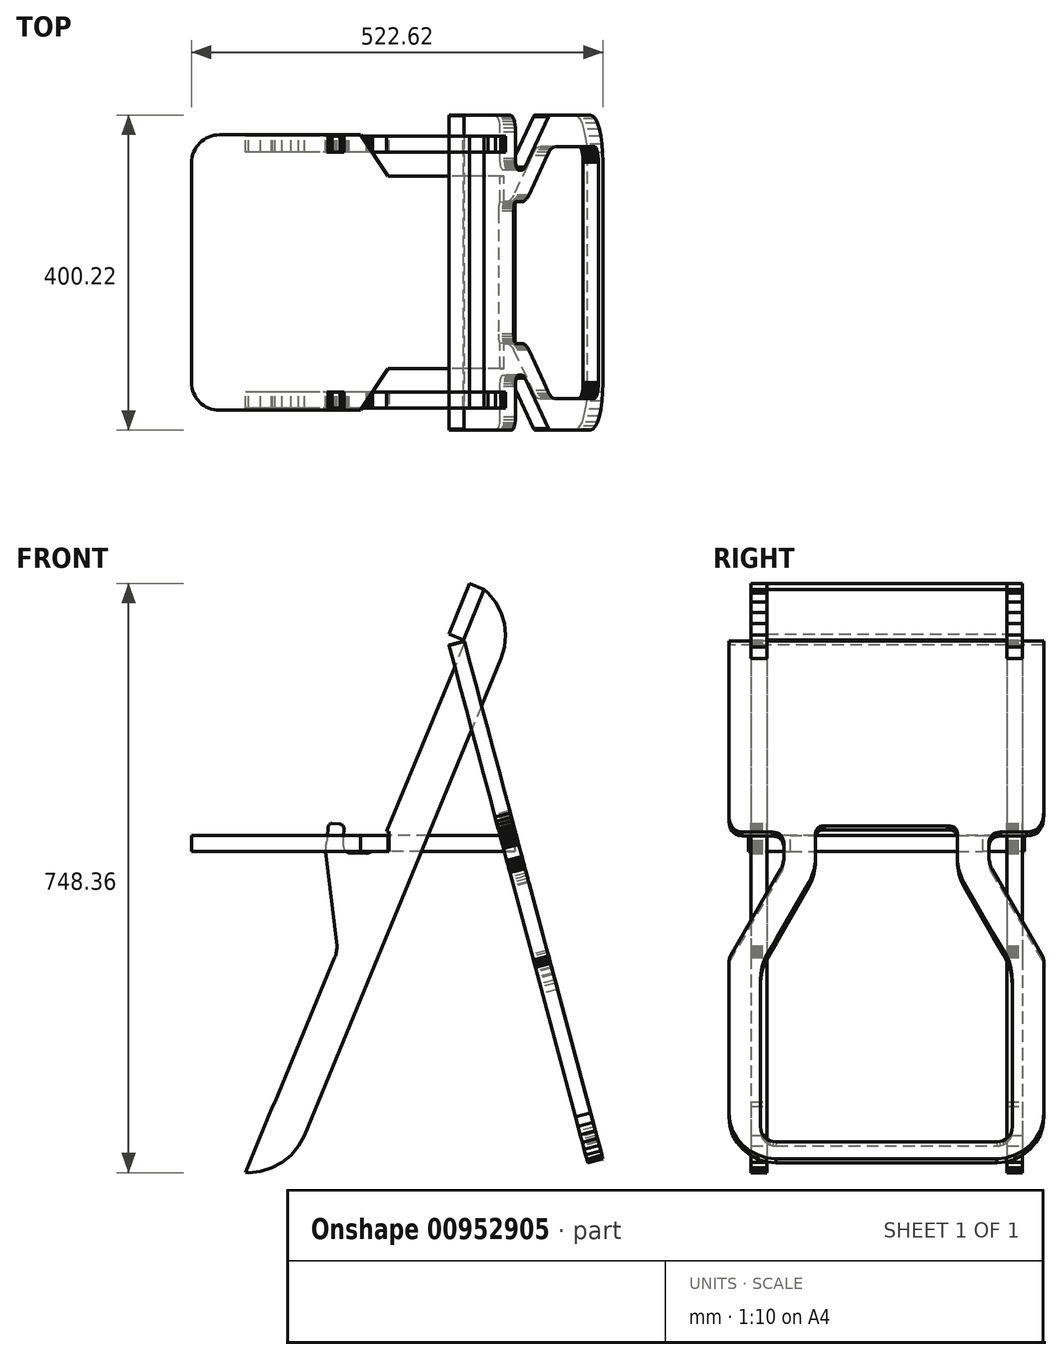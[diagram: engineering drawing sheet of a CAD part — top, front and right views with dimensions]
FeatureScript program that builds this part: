
annotation { "Feature Type Name" : "Feature", "Feature Type Description" : "" }
export const myFeature = defineFeature(function(context is Context, id is Id, definition is map)
    precondition{}
    {
        {
            var Q0;
            Q0=qCreatedBy(makeId("Front.planeOp"),FACE);
            var sketch = newSketch(context, id + "F0", { "sketchPlane" : qUnion([Q0])});
            skLineSegment(sketch, "E0", {"start": v(2007.17, 404.06) * mm, "end": v(2013.51, 402.08) * mm});
            skLineSegment(sketch, "E1", {"start": v(2013.51, 402.08) * mm, "end": v(2026.6, 394.95) * mm});
            skLineSegment(sketch, "E2", {"start": v(2026.6, 394.95) * mm, "end": v(2038.03, 385.51) * mm});
            skLineSegment(sketch, "E3", {"start": v(2038.03, 385.51) * mm, "end": v(2047.46, 374.1) * mm});
            skLineSegment(sketch, "E4", {"start": v(2047.46, 374.1) * mm, "end": v(2054.6, 361) * mm});
            skLineSegment(sketch, "E5", {"start": v(2054.6, 361) * mm, "end": v(2059.1, 346.55) * mm});
            skLineSegment(sketch, "E6", {"start": v(2059.1, 346.55) * mm, "end": v(2060.68, 331.06) * mm});
            skLineSegment(sketch, "E7", {"start": v(2060.68, 331.06) * mm, "end": v(2060.68, -323.77) * mm});
            skLineSegment(sketch, "E8", {"start": v(2060.68, -323.77) * mm, "end": v(2059.1, -339.25) * mm});
            skLineSegment(sketch, "E9", {"start": v(2059.1, -339.25) * mm, "end": v(2054.6, -353.7) * mm});
            skLineSegment(sketch, "E10", {"start": v(2054.6, -353.7) * mm, "end": v(2047.46, -366.8) * mm});
            skLineSegment(sketch, "E11", {"start": v(2047.46, -366.8) * mm, "end": v(2038.03, -378.22) * mm});
            skLineSegment(sketch, "E12", {"start": v(2038.03, -378.22) * mm, "end": v(2026.6, -387.65) * mm});
            skLineSegment(sketch, "E13", {"start": v(2026.6, -387.65) * mm, "end": v(2013.51, -394.78) * mm});
            skLineSegment(sketch, "E14", {"start": v(2013.51, -394.78) * mm, "end": v(2009.8, -395.94) * mm});
            skLineSegment(sketch, "E15", {"start": v(2010.11, -100.23) * mm, "end": v(2010.11, -299.15) * mm});
            skLineSegment(sketch, "E16", {"start": v(2010.11, -299.15) * mm, "end": v(2009.5, -305.2) * mm});
            skLineSegment(sketch, "E17", {"start": v(2007.4, 334.75) * mm, "end": v(2008.19, 333.78) * mm});
            skLineSegment(sketch, "E18", {"start": v(2008.19, 333.78) * mm, "end": v(2009.23, 331.88) * mm});
            skLineSegment(sketch, "E19", {"start": v(2009.23, 331.88) * mm, "end": v(2009.88, 329.78) * mm});
            skLineSegment(sketch, "E20", {"start": v(2009.88, 329.78) * mm, "end": v(2010.11, 327.52) * mm});
            skLineSegment(sketch, "E21", {"start": v(2010.11, 327.52) * mm, "end": v(2010.11, 68.34) * mm});
            skLineSegment(sketch, "E22", {"start": v(2010.11, 68.34) * mm, "end": v(2010.11, 63.22) * mm});
            skLineSegment(sketch, "E23", {"start": v(2010.11, 63.22) * mm, "end": v(2009.48, 58) * mm});
            skLineSegment(sketch, "E24", {"start": v(2009.48, 58) * mm, "end": v(2008.29, 52.92) * mm});
            skLineSegment(sketch, "E25", {"start": v(2008.29, 52.92) * mm, "end": v(2006.6, 48.23) * mm});
            skLineSegment(sketch, "E26", {"start": v(2006.6, 48.23) * mm, "end": v(2004.45, 44.16) * mm});
            skLineSegment(sketch, "E27", {"start": v(2004.45, 44.16) * mm, "end": v(2001.94, 40.95) * mm});
            skLineSegment(sketch, "E28", {"start": v(2001.94, 40.95) * mm, "end": v(1999.1, 38.85) * mm});
            skLineSegment(sketch, "E29", {"start": v(1999.1, 38.85) * mm, "end": v(1996.98, 37.37) * mm});
            skLineSegment(sketch, "E30", {"start": v(1996.98, 37.37) * mm, "end": v(1976.11, 29) * mm});
            skLineSegment(sketch, "E31", {"start": v(1976.11, 29) * mm, "end": v(1973.5, 29.28) * mm});
            skLineSegment(sketch, "E32", {"start": v(1973.5, 29.28) * mm, "end": v(1971.2, 30.06) * mm});
            skLineSegment(sketch, "E33", {"start": v(1971.2, 30.06) * mm, "end": v(1969.22, 31.28) * mm});
            skLineSegment(sketch, "E34", {"start": v(1969.22, 31.28) * mm, "end": v(1967.59, 32.9) * mm});
            skLineSegment(sketch, "E35", {"start": v(1967.59, 32.9) * mm, "end": v(1966.3, 34.84) * mm});
            skLineSegment(sketch, "E36", {"start": v(1966.3, 34.84) * mm, "end": v(1965.37, 37.06) * mm});
            skLineSegment(sketch, "E37", {"start": v(1965.37, 37.06) * mm, "end": v(1958.88, 54.54) * mm});
            skLineSegment(sketch, "E38", {"start": v(1958.88, 54.54) * mm, "end": v(1958.2, 55.86) * mm});
            skLineSegment(sketch, "E39", {"start": v(1958.2, 55.86) * mm, "end": v(1957.45, 56.96) * mm});
            skLineSegment(sketch, "E40", {"start": v(1957.45, 56.96) * mm, "end": v(1956.64, 57.82) * mm});
            skLineSegment(sketch, "E41", {"start": v(1956.64, 57.82) * mm, "end": v(1955.76, 58.45) * mm});
            skLineSegment(sketch, "E42", {"start": v(1955.76, 58.45) * mm, "end": v(1954.82, 58.85) * mm});
            skLineSegment(sketch, "E43", {"start": v(1954.82, 58.85) * mm, "end": v(1953.8, 59.02) * mm});
            skLineSegment(sketch, "E44", {"start": v(1953.8, 59.02) * mm, "end": v(1952.73, 58.96) * mm});
            skLineSegment(sketch, "E45", {"start": v(1952.73, 58.96) * mm, "end": v(1951.59, 58.66) * mm});
            skLineSegment(sketch, "E46", {"start": v(1951.59, 58.66) * mm, "end": v(1942.33, 55.68) * mm});
            skLineSegment(sketch, "E47", {"start": v(1942.33, 55.68) * mm, "end": v(1941.28, 55.24) * mm});
            skLineSegment(sketch, "E48", {"start": v(1941.28, 55.24) * mm, "end": v(1940.44, 54.66) * mm});
            skLineSegment(sketch, "E49", {"start": v(1940.44, 54.66) * mm, "end": v(1939.8, 53.91) * mm});
            skLineSegment(sketch, "E50", {"start": v(1939.8, 53.91) * mm, "end": v(1939.39, 53.02) * mm});
            skLineSegment(sketch, "E51", {"start": v(1939.39, 53.02) * mm, "end": v(1939.17, 51.97) * mm});
            skLineSegment(sketch, "E52", {"start": v(1939.17, 51.97) * mm, "end": v(1939.15, 50.78) * mm});
            skLineSegment(sketch, "E53", {"start": v(1939.15, 50.78) * mm, "end": v(1939.33, 49.45) * mm});
            skLineSegment(sketch, "E54", {"start": v(1939.33, 49.45) * mm, "end": v(1939.7, 47.98) * mm});
            skLineSegment(sketch, "E55", {"start": v(1939.7, 47.98) * mm, "end": v(1944.4, 33.38) * mm});
            skLineSegment(sketch, "E56", {"start": v(1944.4, 33.38) * mm, "end": v(1944.5, 31.68) * mm});
            skLineSegment(sketch, "E57", {"start": v(1944.5, 31.68) * mm, "end": v(1944.7, 30.05) * mm});
            skLineSegment(sketch, "E58", {"start": v(1944.7, 30.05) * mm, "end": v(1944.96, 28.48) * mm});
            skLineSegment(sketch, "E59", {"start": v(1944.96, 28.48) * mm, "end": v(1945.29, 26.96) * mm});
            skLineSegment(sketch, "E60", {"start": v(1945.29, 26.96) * mm, "end": v(1945.68, 25.5) * mm});
            skLineSegment(sketch, "E61", {"start": v(1945.68, 25.5) * mm, "end": v(1946.8, 22.9) * mm});
            skLineSegment(sketch, "E62", {"start": v(1946.8, 22.9) * mm, "end": v(1947.33, 21.55) * mm});
            skLineSegment(sketch, "E63", {"start": v(1947.33, 21.55) * mm, "end": v(1948.2, 19.6) * mm});
            skLineSegment(sketch, "E64", {"start": v(1948.2, 19.6) * mm, "end": v(2007.08, -85.78) * mm});
            skLineSegment(sketch, "E65", {"start": v(2007.08, -85.78) * mm, "end": v(2007.77, -87.31) * mm});
            skLineSegment(sketch, "E66", {"start": v(2007.77, -87.31) * mm, "end": v(2008.37, -88.92) * mm});
            skLineSegment(sketch, "E67", {"start": v(2008.37, -88.92) * mm, "end": v(2008.89, -90.61) * mm});
            skLineSegment(sketch, "E68", {"start": v(2008.89, -90.61) * mm, "end": v(2009.3, -92.38) * mm});
            skLineSegment(sketch, "E69", {"start": v(2009.3, -92.38) * mm, "end": v(2009.64, -94.23) * mm});
            skLineSegment(sketch, "E70", {"start": v(2009.64, -94.23) * mm, "end": v(2009.88, -96.15) * mm});
            skLineSegment(sketch, "E71", {"start": v(2009.88, -96.15) * mm, "end": v(2010.04, -98.16) * mm});
            skLineSegment(sketch, "E72", {"start": v(2010.04, -98.16) * mm, "end": v(2010.11, -100.23) * mm});
            skLineSegment(sketch, "E73", {"start": v(2007.17, 404.06) * mm, "end": v(2007.4, 334.75) * mm});
            skLineSegment(sketch, "E74.trimOffspring", {"start": v(2009.5, -305.2) * mm, "end": v(2009.8, -395.94) * mm});
            skSolve(sketch);
        }
        {
            var Q0;
            Q0=makeQuery(id+"F0.imprint","IMPRINT",FACE,{"disambiguationData":[TD([[makeQuery(id+"F0.imprint","IMPRINT",EDGE,{"derivedFrom":sQuery(id+"F0.wireOp",EDGE,"E0")}),-1.0]])]});
            extrude(context, id + "F1", {"entities" : qUnion([Q0]), "depth" : 20 * mm, "offsetDistance" : 25 * mm});
        }
        {
            var Q0;
            Q0=makeQuery(id+"F1.opExtrude","SWEPT_BODY",BODY,{"disambiguationData":[OSD([sQuery(id+"F0.wireOp",EDGE,"E0"),sQuery(id+"F0.wireOp",EDGE,"E1"),sQuery(id+"F0.wireOp",EDGE,"E2"),sQuery(id+"F0.wireOp",EDGE,"E3"),sQuery(id+"F0.wireOp",EDGE,"E4"),sQuery(id+"F0.wireOp",EDGE,"E5"),sQuery(id+"F0.wireOp",EDGE,"E6"),sQuery(id+"F0.wireOp",EDGE,"E7"),sQuery(id+"F0.wireOp",EDGE,"E8"),sQuery(id+"F0.wireOp",EDGE,"E9"),sQuery(id+"F0.wireOp",EDGE,"E10"),sQuery(id+"F0.wireOp",EDGE,"E11"),sQuery(id+"F0.wireOp",EDGE,"E12"),sQuery(id+"F0.wireOp",EDGE,"E13"),sQuery(id+"F0.wireOp",EDGE,"E14"),sQuery(id+"F0.wireOp",EDGE,"E15"),sQuery(id+"F0.wireOp",EDGE,"E16"),sQuery(id+"F0.wireOp",EDGE,"E17"),sQuery(id+"F0.wireOp",EDGE,"E18"),sQuery(id+"F0.wireOp",EDGE,"E19"),sQuery(id+"F0.wireOp",EDGE,"E20"),sQuery(id+"F0.wireOp",EDGE,"E21"),sQuery(id+"F0.wireOp",EDGE,"E22"),sQuery(id+"F0.wireOp",EDGE,"E23"),sQuery(id+"F0.wireOp",EDGE,"E24"),sQuery(id+"F0.wireOp",EDGE,"E25"),sQuery(id+"F0.wireOp",EDGE,"E26"),sQuery(id+"F0.wireOp",EDGE,"E27"),sQuery(id+"F0.wireOp",EDGE,"E28"),sQuery(id+"F0.wireOp",EDGE,"E29"),sQuery(id+"F0.wireOp",EDGE,"E30"),sQuery(id+"F0.wireOp",EDGE,"E31"),sQuery(id+"F0.wireOp",EDGE,"E32"),sQuery(id+"F0.wireOp",EDGE,"E33"),sQuery(id+"F0.wireOp",EDGE,"E34"),sQuery(id+"F0.wireOp",EDGE,"E35"),sQuery(id+"F0.wireOp",EDGE,"E36"),sQuery(id+"F0.wireOp",EDGE,"bf83b80b-95e6-45bf-b00d-f85eb3b2e45b"),sQuery(id+"F0.wireOp",EDGE,"3aedeaf8-a7c8-49c8-8eb8-d34febc41528"),sQuery(id+"F0.wireOp",EDGE,"E37"),sQuery(id+"F0.wireOp",EDGE,"E38"),sQuery(id+"F0.wireOp",EDGE,"E39"),sQuery(id+"F0.wireOp",EDGE,"E40"),sQuery(id+"F0.wireOp",EDGE,"E41"),sQuery(id+"F0.wireOp",EDGE,"E42"),sQuery(id+"F0.wireOp",EDGE,"E43"),sQuery(id+"F0.wireOp",EDGE,"E44"),sQuery(id+"F0.wireOp",EDGE,"E45"),sQuery(id+"F0.wireOp",EDGE,"E46"),sQuery(id+"F0.wireOp",EDGE,"E47"),sQuery(id+"F0.wireOp",EDGE,"E48"),sQuery(id+"F0.wireOp",EDGE,"E49"),sQuery(id+"F0.wireOp",EDGE,"E50"),sQuery(id+"F0.wireOp",EDGE,"E51"),sQuery(id+"F0.wireOp",EDGE,"E52"),sQuery(id+"F0.wireOp",EDGE,"E53"),sQuery(id+"F0.wireOp",EDGE,"E54"),sQuery(id+"F0.wireOp",EDGE,"E55"),sQuery(id+"F0.wireOp",EDGE,"E56"),sQuery(id+"F0.wireOp",EDGE,"E57"),sQuery(id+"F0.wireOp",EDGE,"E58"),sQuery(id+"F0.wireOp",EDGE,"E59"),sQuery(id+"F0.wireOp",EDGE,"E60"),sQuery(id+"F0.wireOp",EDGE,"E61"),sQuery(id+"F0.wireOp",EDGE,"E62"),sQuery(id+"F0.wireOp",EDGE,"E63"),sQuery(id+"F0.wireOp",EDGE,"E64"),sQuery(id+"F0.wireOp",EDGE,"E65"),sQuery(id+"F0.wireOp",EDGE,"E66"),sQuery(id+"F0.wireOp",EDGE,"E67"),sQuery(id+"F0.wireOp",EDGE,"E68"),sQuery(id+"F0.wireOp",EDGE,"E69"),sQuery(id+"F0.wireOp",EDGE,"E70"),sQuery(id+"F0.wireOp",EDGE,"E71"),sQuery(id+"F0.wireOp",EDGE,"E72"),sQuery(id+"F0.wireOp",EDGE,"E73"),sQuery(id+"F0.wireOp",EDGE,"E74.trimOffspring")])]});
            var Q1;
            Q1=makeQuery(id+"F1.opExtrude","SWEPT_EDGE",EDGE,{"disambiguationData":[OSD([sQuery(id+"F0.wireOp",EDGE,"E14"),sQuery(id+"F0.wireOp",EDGE,"E74.trimOffspring")])]});
            transform(context, id + "F2", {"entities" : qUnion([Q0]), "transformType" : TransformType.ROTATION, "transformAxis" : qUnion([Q1]), "angle" : 0.4 * radian, "makeCopy" : false});
        }
        {
            var Q0;
            Q0=makeQuery(id+"F1.opExtrude","SWEPT_BODY",BODY,{"disambiguationData":[OSD([sQuery(id+"F0.wireOp",EDGE,"E0"),sQuery(id+"F0.wireOp",EDGE,"E1"),sQuery(id+"F0.wireOp",EDGE,"E2"),sQuery(id+"F0.wireOp",EDGE,"E3"),sQuery(id+"F0.wireOp",EDGE,"E4"),sQuery(id+"F0.wireOp",EDGE,"E5"),sQuery(id+"F0.wireOp",EDGE,"E6"),sQuery(id+"F0.wireOp",EDGE,"E7"),sQuery(id+"F0.wireOp",EDGE,"E8"),sQuery(id+"F0.wireOp",EDGE,"E9"),sQuery(id+"F0.wireOp",EDGE,"E10"),sQuery(id+"F0.wireOp",EDGE,"E11"),sQuery(id+"F0.wireOp",EDGE,"E12"),sQuery(id+"F0.wireOp",EDGE,"E13"),sQuery(id+"F0.wireOp",EDGE,"E14"),sQuery(id+"F0.wireOp",EDGE,"E15"),sQuery(id+"F0.wireOp",EDGE,"E16"),sQuery(id+"F0.wireOp",EDGE,"E17"),sQuery(id+"F0.wireOp",EDGE,"E18"),sQuery(id+"F0.wireOp",EDGE,"E19"),sQuery(id+"F0.wireOp",EDGE,"E20"),sQuery(id+"F0.wireOp",EDGE,"E21"),sQuery(id+"F0.wireOp",EDGE,"E22"),sQuery(id+"F0.wireOp",EDGE,"E23"),sQuery(id+"F0.wireOp",EDGE,"E24"),sQuery(id+"F0.wireOp",EDGE,"E25"),sQuery(id+"F0.wireOp",EDGE,"E26"),sQuery(id+"F0.wireOp",EDGE,"E27"),sQuery(id+"F0.wireOp",EDGE,"E28"),sQuery(id+"F0.wireOp",EDGE,"E29"),sQuery(id+"F0.wireOp",EDGE,"E30"),sQuery(id+"F0.wireOp",EDGE,"E31"),sQuery(id+"F0.wireOp",EDGE,"E32"),sQuery(id+"F0.wireOp",EDGE,"E33"),sQuery(id+"F0.wireOp",EDGE,"E34"),sQuery(id+"F0.wireOp",EDGE,"E35"),sQuery(id+"F0.wireOp",EDGE,"E36"),sQuery(id+"F0.wireOp",EDGE,"bf83b80b-95e6-45bf-b00d-f85eb3b2e45b"),sQuery(id+"F0.wireOp",EDGE,"3aedeaf8-a7c8-49c8-8eb8-d34febc41528"),sQuery(id+"F0.wireOp",EDGE,"E37"),sQuery(id+"F0.wireOp",EDGE,"E38"),sQuery(id+"F0.wireOp",EDGE,"E39"),sQuery(id+"F0.wireOp",EDGE,"E40"),sQuery(id+"F0.wireOp",EDGE,"E41"),sQuery(id+"F0.wireOp",EDGE,"E42"),sQuery(id+"F0.wireOp",EDGE,"E43"),sQuery(id+"F0.wireOp",EDGE,"E44"),sQuery(id+"F0.wireOp",EDGE,"E45"),sQuery(id+"F0.wireOp",EDGE,"E46"),sQuery(id+"F0.wireOp",EDGE,"E47"),sQuery(id+"F0.wireOp",EDGE,"E48"),sQuery(id+"F0.wireOp",EDGE,"E49"),sQuery(id+"F0.wireOp",EDGE,"E50"),sQuery(id+"F0.wireOp",EDGE,"E51"),sQuery(id+"F0.wireOp",EDGE,"E52"),sQuery(id+"F0.wireOp",EDGE,"E53"),sQuery(id+"F0.wireOp",EDGE,"E54"),sQuery(id+"F0.wireOp",EDGE,"E55"),sQuery(id+"F0.wireOp",EDGE,"E56"),sQuery(id+"F0.wireOp",EDGE,"E57"),sQuery(id+"F0.wireOp",EDGE,"E58"),sQuery(id+"F0.wireOp",EDGE,"E59"),sQuery(id+"F0.wireOp",EDGE,"E60"),sQuery(id+"F0.wireOp",EDGE,"E61"),sQuery(id+"F0.wireOp",EDGE,"E62"),sQuery(id+"F0.wireOp",EDGE,"E63"),sQuery(id+"F0.wireOp",EDGE,"E64"),sQuery(id+"F0.wireOp",EDGE,"E65"),sQuery(id+"F0.wireOp",EDGE,"E66"),sQuery(id+"F0.wireOp",EDGE,"E67"),sQuery(id+"F0.wireOp",EDGE,"E68"),sQuery(id+"F0.wireOp",EDGE,"E69"),sQuery(id+"F0.wireOp",EDGE,"E70"),sQuery(id+"F0.wireOp",EDGE,"E71"),sQuery(id+"F0.wireOp",EDGE,"E72"),sQuery(id+"F0.wireOp",EDGE,"E73"),sQuery(id+"F0.wireOp",EDGE,"E74.trimOffspring")])]});
            transform(context, id + "F3", {"entities" : qUnion([Q0]), "transformType" : TransformType.TRANSLATION_3D, "dx" : -2060 * mm, "dy" : 0 * mm, "dz" : 0 * mm, "makeCopy" : false});
        }
        {
            var Q0;
            Q0=qCreatedBy(makeId("Top.planeOp"),FACE);
            cPlane(context, id + "F4", {"entities" : qUnion([Q0]), "cplaneType" : CPlaneType.OFFSET, "offset" : 12 * mm, "width" : 150 * mm, "height" : 150 * mm});
        }
        {
            var Q0;
            Q0=qCreatedBy(id+"F4.planeOp",FACE);
            var sketch = newSketch(context, id + "F5", { "sketchPlane" : qUnion([Q0])});
            skLineSegment(sketch, "E75.bottom", {"start": v(95.33, 327) * mm, "end": v(-83.33, 327) * mm});
            skLineSegment(sketch, "E75.top", {"start": v(95.33, -23) * mm, "end": v(-83.33, -23) * mm});
            skLineSegment(sketch, "E75.left", {"start": v(131, 291.33) * mm, "end": v(131, 12.67) * mm});
            skLineSegment(sketch, "E75.right", {"start": v(-119, 291.33) * mm, "end": v(-119, 12.67) * mm});
            skPoint(sketch, "E76.visualSharp", {"position": v(-119, 327) * mm});
            skArc(sketch, "E76.filletArc", {"start": v(-83.33, 327) * mm, "mid": v(-108.55, 316.55) * mm, "end": v(-119, 291.33) * mm});
            skPoint(sketch, "E77.visualSharp", {"position": v(131, 327) * mm});
            skArc(sketch, "E77.filletArc", {"start": v(131, 291.33) * mm, "mid": v(120.55, 316.55) * mm, "end": v(95.33, 327) * mm});
            skPoint(sketch, "E78.visualSharp", {"position": v(131, -23) * mm});
            skArc(sketch, "E78.filletArc", {"start": v(95.33, -23) * mm, "mid": v(120.55, -12.55) * mm, "end": v(131, 12.67) * mm});
            skPoint(sketch, "E79.visualSharp", {"position": v(-119, -23) * mm});
            skArc(sketch, "E79.filletArc", {"start": v(-119, 12.67) * mm, "mid": v(-108.55, -12.55) * mm, "end": v(-83.33, -23) * mm});
            skSolve(sketch);
        }
        {
            var Q0;
            Q0=makeQuery(id+"F5.imprint","IMPRINT",FACE,{"disambiguationData":[TD([[makeQuery(id+"F5.imprint","IMPRINT",EDGE,{"derivedFrom":sQuery(id+"F5.wireOp",EDGE,"E75.bottom")}),1.0]])]});
            extrude(context, id + "F6", {"entities" : qUnion([Q0]), "depth" : 20 * mm, "offsetDistance" : 25 * mm});
        }
        {
            var Q0;
            Q0=makeQuery(id+"F1.opExtrude","SWEPT_BODY",BODY,{"disambiguationData":[OSD([sQuery(id+"F0.wireOp",EDGE,"E0"),sQuery(id+"F0.wireOp",EDGE,"E1"),sQuery(id+"F0.wireOp",EDGE,"E2"),sQuery(id+"F0.wireOp",EDGE,"E3"),sQuery(id+"F0.wireOp",EDGE,"E4"),sQuery(id+"F0.wireOp",EDGE,"E5"),sQuery(id+"F0.wireOp",EDGE,"E6"),sQuery(id+"F0.wireOp",EDGE,"E7"),sQuery(id+"F0.wireOp",EDGE,"E8"),sQuery(id+"F0.wireOp",EDGE,"E9"),sQuery(id+"F0.wireOp",EDGE,"E10"),sQuery(id+"F0.wireOp",EDGE,"E11"),sQuery(id+"F0.wireOp",EDGE,"E12"),sQuery(id+"F0.wireOp",EDGE,"E13"),sQuery(id+"F0.wireOp",EDGE,"E14"),sQuery(id+"F0.wireOp",EDGE,"E15"),sQuery(id+"F0.wireOp",EDGE,"E16"),sQuery(id+"F0.wireOp",EDGE,"E17"),sQuery(id+"F0.wireOp",EDGE,"E18"),sQuery(id+"F0.wireOp",EDGE,"E19"),sQuery(id+"F0.wireOp",EDGE,"E20"),sQuery(id+"F0.wireOp",EDGE,"E21"),sQuery(id+"F0.wireOp",EDGE,"E22"),sQuery(id+"F0.wireOp",EDGE,"E23"),sQuery(id+"F0.wireOp",EDGE,"E24"),sQuery(id+"F0.wireOp",EDGE,"E25"),sQuery(id+"F0.wireOp",EDGE,"E26"),sQuery(id+"F0.wireOp",EDGE,"E27"),sQuery(id+"F0.wireOp",EDGE,"E28"),sQuery(id+"F0.wireOp",EDGE,"E29"),sQuery(id+"F0.wireOp",EDGE,"E30"),sQuery(id+"F0.wireOp",EDGE,"E31"),sQuery(id+"F0.wireOp",EDGE,"E32"),sQuery(id+"F0.wireOp",EDGE,"E33"),sQuery(id+"F0.wireOp",EDGE,"E34"),sQuery(id+"F0.wireOp",EDGE,"E35"),sQuery(id+"F0.wireOp",EDGE,"E36"),sQuery(id+"F0.wireOp",EDGE,"E37"),sQuery(id+"F0.wireOp",EDGE,"E38"),sQuery(id+"F0.wireOp",EDGE,"E39"),sQuery(id+"F0.wireOp",EDGE,"E40"),sQuery(id+"F0.wireOp",EDGE,"E41"),sQuery(id+"F0.wireOp",EDGE,"E42"),sQuery(id+"F0.wireOp",EDGE,"E43"),sQuery(id+"F0.wireOp",EDGE,"E44"),sQuery(id+"F0.wireOp",EDGE,"E45"),sQuery(id+"F0.wireOp",EDGE,"E46"),sQuery(id+"F0.wireOp",EDGE,"E47"),sQuery(id+"F0.wireOp",EDGE,"E48"),sQuery(id+"F0.wireOp",EDGE,"E49"),sQuery(id+"F0.wireOp",EDGE,"E50"),sQuery(id+"F0.wireOp",EDGE,"E51"),sQuery(id+"F0.wireOp",EDGE,"E52"),sQuery(id+"F0.wireOp",EDGE,"E53"),sQuery(id+"F0.wireOp",EDGE,"E54"),sQuery(id+"F0.wireOp",EDGE,"E55"),sQuery(id+"F0.wireOp",EDGE,"E56"),sQuery(id+"F0.wireOp",EDGE,"E57"),sQuery(id+"F0.wireOp",EDGE,"E58"),sQuery(id+"F0.wireOp",EDGE,"E59"),sQuery(id+"F0.wireOp",EDGE,"E60"),sQuery(id+"F0.wireOp",EDGE,"E61"),sQuery(id+"F0.wireOp",EDGE,"E62"),sQuery(id+"F0.wireOp",EDGE,"E63"),sQuery(id+"F0.wireOp",EDGE,"E64"),sQuery(id+"F0.wireOp",EDGE,"E65"),sQuery(id+"F0.wireOp",EDGE,"E66"),sQuery(id+"F0.wireOp",EDGE,"E67"),sQuery(id+"F0.wireOp",EDGE,"E68"),sQuery(id+"F0.wireOp",EDGE,"E69"),sQuery(id+"F0.wireOp",EDGE,"E70"),sQuery(id+"F0.wireOp",EDGE,"E71"),sQuery(id+"F0.wireOp",EDGE,"E72"),sQuery(id+"F0.wireOp",EDGE,"E73"),sQuery(id+"F0.wireOp",EDGE,"E74.trimOffspring")])]});
            transform(context, id + "F7", {"entities" : qUnion([Q0]), "transformType" : TransformType.TRANSLATION_3D, "dx" : 0 * mm, "dy" : 325 * mm, "dz" : 0 * mm, "makeCopy" : true});
        }
        {
            var Q0;
            Q0=qCreatedBy(id+"F4.planeOp",FACE);
            var sketch = newSketch(context, id + "F8", { "sketchPlane" : qUnion([Q0])});
            skLineSegment(sketch, "E80", {"start": v(95.42, -22.88) * mm, "end": v(132.24, 31.84) * mm});
            skLineSegment(sketch, "E81", {"start": v(132.24, 31.84) * mm, "end": v(131.7, -45.16) * mm});
            skLineSegment(sketch, "E82", {"start": v(131.7, -45.16) * mm, "end": v(95.42, -22.88) * mm});
            skLineSegment(sketch, "E83.MirrorCS", {"start": v(132.24, 272.56) * mm, "end": v(131.7, 349.56) * mm});
            skLineSegment(sketch, "E84.MirrorCS", {"start": v(131.7, 349.56) * mm, "end": v(95.42, 327.28) * mm});
            skLineSegment(sketch, "E85.MirrorCS", {"start": v(95.42, 327.28) * mm, "end": v(132.24, 272.56) * mm});
            skSolve(sketch);
        }
        {
            var Q0;
            Q0=makeQuery(id+"F8.imprint","IMPRINT",FACE,{"disambiguationData":[TD([[makeQuery(id+"F8.imprint","IMPRINT",EDGE,{"derivedFrom":sQuery(id+"F8.wireOp",EDGE,"E80")}),-1.0]])]});
            var Q1;
            Q1=makeQuery(id+"F8.imprint","IMPRINT",FACE,{"disambiguationData":[TD([[makeQuery(id+"F8.imprint","IMPRINT",EDGE,{"derivedFrom":sQuery(id+"F8.wireOp",EDGE,"E83.MirrorCS")}),1.0]])]});
            extrude(context, id + "F9", {"entities" : qUnion([Q0, Q1]), "operationType" : NewBodyOperationType.REMOVE, "depth" : 25 * mm, "offsetDistance" : 25 * mm});
        }
        {
            var Q0;
            Q0=makeQuery(id+"F7.opPattern","COPY",FACE,{"derivedFrom":makeQuery(id+"F1.opExtrude","SWEPT_FACE",FACE,{"disambiguationData":[OSD([sQuery(id+"F0.wireOp",EDGE,"E73")])]}),"instanceName":"1"});
            var Q1;
            Q1=makeQuery(id+"F1.opExtrude","SWEPT_FACE",FACE,{"disambiguationData":[OSD([sQuery(id+"F0.wireOp",EDGE,"E73")])]});
            extrude(context, id + "F10", {"entities" : qUnion([Q0, Q1]), "depth" : 20 * mm, "offsetDistance" : 25 * mm});
        }
        {
            var Q0;
            {var subQ0=sQuery(id+"F0.wireOp",EDGE,"E73");Q0=makeQuery(id+"F10.opExtrude","SWEPT_FACE",FACE,{"disambiguationData":[OSD([subQ0]),TDD([makeQuery(id+"F1.opExtrude","CAP_EDGE",EDGE,{"disambiguationData":[OSD([subQ0])],"isStart":true})])]});}
            var Q1;
            {var subQ0=sQuery(id+"F0.wireOp",EDGE,"E73");Q1=makeQuery(id+"F10.opExtrude","SWEPT_FACE",FACE,{"disambiguationData":[OSD([subQ0]),TDD([makeQuery(id+"F7.opPattern","COPY",EDGE,{"derivedFrom":makeQuery(id+"F1.opExtrude","CAP_EDGE",EDGE,{"disambiguationData":[OSD([subQ0])],"isStart":false}),"instanceName":"1"})])]});}
            loft(context, id + "F11", {"sheetProfilesArray" : [{ "sheetProfileEntities" : qUnion([Q0]) }, { "sheetProfileEntities" : qUnion([Q1]) }]});
        }
        {
            var Q0;
            Q0=qCreatedBy(makeId("Right.planeOp"),FACE);
            var sketch = newSketch(context, id + "F12", { "sketchPlane" : qUnion([Q0])});
            skLineSegment(sketch, "E86", {"start": v(183.85, 400.19) * mm, "end": v(199.17, 398.63) * mm});
            skLineSegment(sketch, "E87", {"start": v(199.17, 398.63) * mm, "end": v(213.46, 394.17) * mm});
            skLineSegment(sketch, "E88", {"start": v(213.46, 394.17) * mm, "end": v(226.42, 387.12) * mm});
            skLineSegment(sketch, "E89", {"start": v(226.42, 387.12) * mm, "end": v(237.72, 377.78) * mm});
            skLineSegment(sketch, "E90", {"start": v(237.72, 377.78) * mm, "end": v(247.05, 366.48) * mm});
            skLineSegment(sketch, "E91", {"start": v(247.05, 366.48) * mm, "end": v(254.1, 353.53) * mm});
            skLineSegment(sketch, "E92", {"start": v(254.1, 353.53) * mm, "end": v(258.57, 339.24) * mm});
            skLineSegment(sketch, "E93", {"start": v(258.57, 339.24) * mm, "end": v(260.12, 323.91) * mm});
            skLineSegment(sketch, "E94", {"start": v(260.12, -323.91) * mm, "end": v(258.57, -339.24) * mm});
            skLineSegment(sketch, "E95", {"start": v(258.57, -339.24) * mm, "end": v(254.1, -353.53) * mm});
            skLineSegment(sketch, "E96", {"start": v(254.1, -353.53) * mm, "end": v(247.05, -366.48) * mm});
            skLineSegment(sketch, "E97", {"start": v(247.05, -366.48) * mm, "end": v(237.72, -377.78) * mm});
            skLineSegment(sketch, "E98", {"start": v(237.72, -377.78) * mm, "end": v(226.42, -387.12) * mm});
            skLineSegment(sketch, "E99", {"start": v(226.42, -387.12) * mm, "end": v(213.46, -394.17) * mm});
            skLineSegment(sketch, "E100", {"start": v(213.46, -394.17) * mm, "end": v(199.17, -398.63) * mm});
            skLineSegment(sketch, "E101", {"start": v(199.17, -398.63) * mm, "end": v(183.85, -400.19) * mm});
            skLineSegment(sketch, "E102", {"start": v(-183.85, -400.19) * mm, "end": v(-199.17, -398.63) * mm});
            skLineSegment(sketch, "E103", {"start": v(-199.17, -398.63) * mm, "end": v(-213.46, -394.17) * mm});
            skLineSegment(sketch, "E104", {"start": v(-213.46, -394.17) * mm, "end": v(-226.42, -387.12) * mm});
            skLineSegment(sketch, "E105", {"start": v(-226.42, -387.12) * mm, "end": v(-237.72, -377.78) * mm});
            skLineSegment(sketch, "E106", {"start": v(-237.72, -377.78) * mm, "end": v(-247.05, -366.48) * mm});
            skLineSegment(sketch, "E107", {"start": v(-247.05, -366.48) * mm, "end": v(-254.1, -353.53) * mm});
            skLineSegment(sketch, "E108", {"start": v(-254.1, -353.53) * mm, "end": v(-258.57, -339.24) * mm});
            skLineSegment(sketch, "E109", {"start": v(-258.57, -339.24) * mm, "end": v(-260.12, -323.91) * mm});
            skLineSegment(sketch, "E110", {"start": v(-260.12, 323.91) * mm, "end": v(-258.57, 339.24) * mm});
            skLineSegment(sketch, "E111", {"start": v(-258.57, 339.24) * mm, "end": v(-254.1, 353.53) * mm});
            skLineSegment(sketch, "E112", {"start": v(-254.1, 353.53) * mm, "end": v(-247.05, 366.48) * mm});
            skLineSegment(sketch, "E113", {"start": v(-247.05, 366.48) * mm, "end": v(-237.72, 377.78) * mm});
            skLineSegment(sketch, "E114", {"start": v(-237.72, 377.78) * mm, "end": v(-226.42, 387.12) * mm});
            skLineSegment(sketch, "E115", {"start": v(-226.42, 387.12) * mm, "end": v(-213.46, 394.17) * mm});
            skLineSegment(sketch, "E116", {"start": v(-213.46, 394.17) * mm, "end": v(-199.17, 398.63) * mm});
            skLineSegment(sketch, "E117", {"start": v(-199.17, 398.63) * mm, "end": v(-183.85, 400.19) * mm});
            skLineSegment(sketch, "E118", {"start": v(210.1, -299.56) * mm, "end": v(208.67, -313.63) * mm});
            skLineSegment(sketch, "E119", {"start": v(208.67, -313.63) * mm, "end": v(204.57, -326.75) * mm});
            skLineSegment(sketch, "E120", {"start": v(204.57, -326.75) * mm, "end": v(198.1, -338.65) * mm});
            skLineSegment(sketch, "E121", {"start": v(198.1, -338.65) * mm, "end": v(189.53, -349.02) * mm});
            skLineSegment(sketch, "E122", {"start": v(189.53, -349.02) * mm, "end": v(179.15, -357.6) * mm});
            skLineSegment(sketch, "E123", {"start": v(179.15, -357.6) * mm, "end": v(167.26, -364.07) * mm});
            skLineSegment(sketch, "E124", {"start": v(167.26, -364.07) * mm, "end": v(154.13, -368.16) * mm});
            skLineSegment(sketch, "E125", {"start": v(154.13, -368.16) * mm, "end": v(140.07, -369.6) * mm});
            skLineSegment(sketch, "E126", {"start": v(-140.07, -369.6) * mm, "end": v(-154.13, -368.16) * mm});
            skLineSegment(sketch, "E127", {"start": v(-154.13, -368.16) * mm, "end": v(-167.26, -364.07) * mm});
            skLineSegment(sketch, "E128", {"start": v(-167.26, -364.07) * mm, "end": v(-179.15, -357.6) * mm});
            skLineSegment(sketch, "E129", {"start": v(-179.15, -357.6) * mm, "end": v(-189.53, -349.02) * mm});
            skLineSegment(sketch, "E130", {"start": v(-189.53, -349.02) * mm, "end": v(-198.1, -338.65) * mm});
            skLineSegment(sketch, "E131", {"start": v(-198.1, -338.65) * mm, "end": v(-204.57, -326.75) * mm});
            skLineSegment(sketch, "E132", {"start": v(-204.57, -326.75) * mm, "end": v(-208.67, -313.63) * mm});
            skLineSegment(sketch, "E133", {"start": v(-208.67, -313.63) * mm, "end": v(-210.1, -299.56) * mm});
            skLineSegment(sketch, "E134", {"start": v(-210.1, -102.77) * mm, "end": v(-210.03, -100.72) * mm});
            skLineSegment(sketch, "E135", {"start": v(-210.03, -100.72) * mm, "end": v(-209.87, -98.74) * mm});
            skLineSegment(sketch, "E136", {"start": v(-209.87, -98.74) * mm, "end": v(-209.63, -96.83) * mm});
            skLineSegment(sketch, "E137", {"start": v(-209.63, -96.83) * mm, "end": v(-209.3, -95) * mm});
            skLineSegment(sketch, "E138", {"start": v(-209.3, -95) * mm, "end": v(-208.89, -93.25) * mm});
            skLineSegment(sketch, "E139", {"start": v(-208.89, -93.25) * mm, "end": v(-208.38, -91.58) * mm});
            skLineSegment(sketch, "E140", {"start": v(-208.38, -91.58) * mm, "end": v(-207.78, -89.99) * mm});
            skLineSegment(sketch, "E141", {"start": v(-207.78, -89.99) * mm, "end": v(-207.1, -88.47) * mm});
            skLineSegment(sketch, "E142", {"start": v(-207.1, -88.47) * mm, "end": v(-142.89, 26.6) * mm});
            skLineSegment(sketch, "E143", {"start": v(-142.89, 26.6) * mm, "end": v(-142.31, 27.88) * mm});
            skLineSegment(sketch, "E144", {"start": v(-142.31, 27.88) * mm, "end": v(-141.8, 29.22) * mm});
            skLineSegment(sketch, "E145", {"start": v(-141.8, 29.22) * mm, "end": v(-141.34, 30.61) * mm});
            skLineSegment(sketch, "E146", {"start": v(-141.34, 30.61) * mm, "end": v(-140.95, 32.06) * mm});
            skLineSegment(sketch, "E147", {"start": v(-140.95, 32.06) * mm, "end": v(-140.62, 33.56) * mm});
            skLineSegment(sketch, "E148", {"start": v(-140.62, 33.56) * mm, "end": v(-140.36, 35.11) * mm});
            skLineSegment(sketch, "E149", {"start": v(-140.36, 35.11) * mm, "end": v(-140.18, 36.73) * mm});
            skLineSegment(sketch, "E150", {"start": v(-140.18, 36.73) * mm, "end": v(-140.07, 38.4) * mm});
            skLineSegment(sketch, "E151", {"start": v(-140.07, 38.4) * mm, "end": v(-140.07, 53.59) * mm});
            skLineSegment(sketch, "E152", {"start": v(-140.07, 53.59) * mm, "end": v(-140.17, 55.08) * mm});
            skLineSegment(sketch, "E153", {"start": v(-140.17, 55.08) * mm, "end": v(-140.4, 56.39) * mm});
            skLineSegment(sketch, "E154", {"start": v(-140.4, 56.39) * mm, "end": v(-140.78, 57.5) * mm});
            skLineSegment(sketch, "E155", {"start": v(-140.78, 57.5) * mm, "end": v(-141.3, 58.42) * mm});
            skLineSegment(sketch, "E156", {"start": v(-141.3, 58.42) * mm, "end": v(-141.97, 59.13) * mm});
            skLineSegment(sketch, "E157", {"start": v(-141.97, 59.13) * mm, "end": v(-142.79, 59.64) * mm});
            skLineSegment(sketch, "E158", {"start": v(-142.79, 59.64) * mm, "end": v(-143.76, 59.94) * mm});
            skLineSegment(sketch, "E159", {"start": v(-143.76, 59.94) * mm, "end": v(-144.89, 60.03) * mm});
            skLineSegment(sketch, "E160", {"start": v(-144.89, 60.03) * mm, "end": v(-154.5, 60.03) * mm});
            skLineSegment(sketch, "E161", {"start": v(-154.5, 60.03) * mm, "end": v(-155.67, 59.96) * mm});
            skLineSegment(sketch, "E162", {"start": v(-155.67, 59.96) * mm, "end": v(-156.7, 59.7) * mm});
            skLineSegment(sketch, "E163", {"start": v(-156.7, 59.7) * mm, "end": v(-157.6, 59.23) * mm});
            skLineSegment(sketch, "E164", {"start": v(-157.6, 59.23) * mm, "end": v(-158.37, 58.57) * mm});
            skLineSegment(sketch, "E165", {"start": v(-158.37, 58.57) * mm, "end": v(-159, 57.7) * mm});
            skLineSegment(sketch, "E166", {"start": v(-159, 57.7) * mm, "end": v(-159.5, 56.65) * mm});
            skLineSegment(sketch, "E167", {"start": v(-159.5, 56.65) * mm, "end": v(-159.88, 55.4) * mm});
            skLineSegment(sketch, "E168", {"start": v(-159.88, 55.4) * mm, "end": v(-160.12, 53.94) * mm});
            skLineSegment(sketch, "E169", {"start": v(-160.12, 53.94) * mm, "end": v(-160.09, 47.06) * mm});
            skLineSegment(sketch, "E170", {"start": v(-160.09, 47.06) * mm, "end": v(-160.27, 44.47) * mm});
            skLineSegment(sketch, "E171", {"start": v(-160.27, 44.47) * mm, "end": v(-160.82, 42.05) * mm});
            skLineSegment(sketch, "E172", {"start": v(-160.82, 42.05) * mm, "end": v(-161.74, 39.85) * mm});
            skLineSegment(sketch, "E173", {"start": v(-161.74, 39.85) * mm, "end": v(-163, 37.92) * mm});
            skLineSegment(sketch, "E174", {"start": v(-163, 37.92) * mm, "end": v(-164.63, 36.33) * mm});
            skLineSegment(sketch, "E175", {"start": v(-164.63, 36.33) * mm, "end": v(-166.58, 35.12) * mm});
            skLineSegment(sketch, "E176", {"start": v(-166.58, 35.12) * mm, "end": v(-168.85, 34.35) * mm});
            skLineSegment(sketch, "E177", {"start": v(-168.85, 34.35) * mm, "end": v(-171.44, 34.08) * mm});
            skLineSegment(sketch, "E178", {"start": v(-171.44, 34.08) * mm, "end": v(-196.15, 34.08) * mm});
            skLineSegment(sketch, "E179", {"start": v(-196.15, 34.08) * mm, "end": v(-199.2, 34.82) * mm});
            skLineSegment(sketch, "E180", {"start": v(-199.2, 34.82) * mm, "end": v(-202.01, 36.9) * mm});
            skLineSegment(sketch, "E181", {"start": v(-202.01, 36.9) * mm, "end": v(-204.5, 40.08) * mm});
            skLineSegment(sketch, "E182", {"start": v(-204.5, 40.08) * mm, "end": v(-206.62, 44.1) * mm});
            skLineSegment(sketch, "E183", {"start": v(-206.62, 44.1) * mm, "end": v(-208.3, 48.75) * mm});
            skLineSegment(sketch, "E184", {"start": v(-208.3, 48.75) * mm, "end": v(-209.48, 53.77) * mm});
            skLineSegment(sketch, "E185", {"start": v(-209.48, 53.77) * mm, "end": v(-210.1, 58.93) * mm});
            skLineSegment(sketch, "E186", {"start": v(-210.1, 58.93) * mm, "end": v(-210.1, 64) * mm});
            skLineSegment(sketch, "E187", {"start": v(-210.1, 64) * mm, "end": v(-210.1, 320.41) * mm});
            skLineSegment(sketch, "E188", {"start": v(-210.1, 320.41) * mm, "end": v(-209.87, 322.64) * mm});
            skLineSegment(sketch, "E189", {"start": v(-209.87, 322.64) * mm, "end": v(-209.22, 324.72) * mm});
            skLineSegment(sketch, "E190", {"start": v(-209.22, 324.72) * mm, "end": v(-208.2, 326.6) * mm});
            skLineSegment(sketch, "E191", {"start": v(-208.2, 326.6) * mm, "end": v(-206.84, 328.25) * mm});
            skLineSegment(sketch, "E192", {"start": v(-206.84, 328.25) * mm, "end": v(-205.2, 329.6) * mm});
            skLineSegment(sketch, "E193", {"start": v(-205.2, 329.6) * mm, "end": v(-203.3, 330.64) * mm});
            skLineSegment(sketch, "E194", {"start": v(-203.3, 330.64) * mm, "end": v(-201.23, 331.29) * mm});
            skLineSegment(sketch, "E195", {"start": v(-201.23, 331.29) * mm, "end": v(-199, 331.51) * mm});
            skLineSegment(sketch, "E196", {"start": v(-199, 331.51) * mm, "end": v(199, 331.51) * mm});
            skLineSegment(sketch, "E197", {"start": v(199, 331.51) * mm, "end": v(201.23, 331.29) * mm});
            skLineSegment(sketch, "E198", {"start": v(201.23, 331.29) * mm, "end": v(203.3, 330.64) * mm});
            skLineSegment(sketch, "E199", {"start": v(203.3, 330.64) * mm, "end": v(205.2, 329.6) * mm});
            skLineSegment(sketch, "E200", {"start": v(205.2, 329.6) * mm, "end": v(206.84, 328.25) * mm});
            skLineSegment(sketch, "E201", {"start": v(206.84, 328.25) * mm, "end": v(208.2, 326.6) * mm});
            skLineSegment(sketch, "E202", {"start": v(208.2, 326.6) * mm, "end": v(209.22, 324.72) * mm});
            skLineSegment(sketch, "E203", {"start": v(209.22, 324.72) * mm, "end": v(209.87, 322.64) * mm});
            skLineSegment(sketch, "E204", {"start": v(209.87, 322.64) * mm, "end": v(210.1, 320.41) * mm});
            skLineSegment(sketch, "E205", {"start": v(210.1, 320.41) * mm, "end": v(210.1, 64) * mm});
            skLineSegment(sketch, "E206", {"start": v(210.1, 64) * mm, "end": v(210.1, 58.93) * mm});
            skLineSegment(sketch, "E207", {"start": v(210.1, 58.93) * mm, "end": v(209.48, 53.77) * mm});
            skLineSegment(sketch, "E208", {"start": v(209.48, 53.77) * mm, "end": v(208.3, 48.75) * mm});
            skLineSegment(sketch, "E209", {"start": v(208.3, 48.75) * mm, "end": v(206.62, 44.1) * mm});
            skLineSegment(sketch, "E210", {"start": v(206.62, 44.1) * mm, "end": v(204.5, 40.08) * mm});
            skLineSegment(sketch, "E211", {"start": v(204.5, 40.08) * mm, "end": v(202.01, 36.9) * mm});
            skLineSegment(sketch, "E212", {"start": v(202.01, 36.9) * mm, "end": v(199.2, 34.82) * mm});
            skLineSegment(sketch, "E213", {"start": v(199.2, 34.82) * mm, "end": v(196.15, 34.08) * mm});
            skLineSegment(sketch, "E214", {"start": v(196.15, 34.08) * mm, "end": v(171.44, 34.08) * mm});
            skLineSegment(sketch, "E215", {"start": v(171.44, 34.08) * mm, "end": v(168.85, 34.35) * mm});
            skLineSegment(sketch, "E216", {"start": v(168.85, 34.35) * mm, "end": v(166.58, 35.12) * mm});
            skLineSegment(sketch, "E217", {"start": v(166.58, 35.12) * mm, "end": v(164.63, 36.33) * mm});
            skLineSegment(sketch, "E218", {"start": v(164.63, 36.33) * mm, "end": v(163, 37.92) * mm});
            skLineSegment(sketch, "E219", {"start": v(163, 37.92) * mm, "end": v(161.74, 39.85) * mm});
            skLineSegment(sketch, "E220", {"start": v(161.74, 39.85) * mm, "end": v(160.82, 42.05) * mm});
            skLineSegment(sketch, "E221", {"start": v(160.82, 42.05) * mm, "end": v(160.27, 44.47) * mm});
            skLineSegment(sketch, "E222", {"start": v(160.27, 44.47) * mm, "end": v(160.09, 47.06) * mm});
            skLineSegment(sketch, "E223", {"start": v(160.09, 47.06) * mm, "end": v(160.12, 53.94) * mm});
            skLineSegment(sketch, "E224", {"start": v(160.12, 53.94) * mm, "end": v(159.88, 55.4) * mm});
            skLineSegment(sketch, "E225", {"start": v(159.88, 55.4) * mm, "end": v(159.5, 56.65) * mm});
            skLineSegment(sketch, "E226", {"start": v(159.5, 56.65) * mm, "end": v(159, 57.7) * mm});
            skLineSegment(sketch, "E227", {"start": v(159, 57.7) * mm, "end": v(158.37, 58.57) * mm});
            skLineSegment(sketch, "E228", {"start": v(158.37, 58.57) * mm, "end": v(157.6, 59.23) * mm});
            skLineSegment(sketch, "E229", {"start": v(157.6, 59.23) * mm, "end": v(156.7, 59.7) * mm});
            skLineSegment(sketch, "E230", {"start": v(156.7, 59.7) * mm, "end": v(155.67, 59.96) * mm});
            skLineSegment(sketch, "E231", {"start": v(155.67, 59.96) * mm, "end": v(154.5, 60.03) * mm});
            skLineSegment(sketch, "E232", {"start": v(154.5, 60.03) * mm, "end": v(144.89, 60.03) * mm});
            skLineSegment(sketch, "E233", {"start": v(144.89, 60.03) * mm, "end": v(143.76, 59.94) * mm});
            skLineSegment(sketch, "E234", {"start": v(143.76, 59.94) * mm, "end": v(142.79, 59.64) * mm});
            skLineSegment(sketch, "E235", {"start": v(142.79, 59.64) * mm, "end": v(141.97, 59.13) * mm});
            skLineSegment(sketch, "E236", {"start": v(141.97, 59.13) * mm, "end": v(141.3, 58.42) * mm});
            skLineSegment(sketch, "E237", {"start": v(141.3, 58.42) * mm, "end": v(140.78, 57.5) * mm});
            skLineSegment(sketch, "E238", {"start": v(140.78, 57.5) * mm, "end": v(140.4, 56.39) * mm});
            skLineSegment(sketch, "E239", {"start": v(140.4, 56.39) * mm, "end": v(140.17, 55.08) * mm});
            skLineSegment(sketch, "E240", {"start": v(140.17, 55.08) * mm, "end": v(140.07, 53.59) * mm});
            skLineSegment(sketch, "E241", {"start": v(140.07, 53.59) * mm, "end": v(140.07, 38.4) * mm});
            skLineSegment(sketch, "E242", {"start": v(140.07, 38.4) * mm, "end": v(140.18, 36.73) * mm});
            skLineSegment(sketch, "E243", {"start": v(140.18, 36.73) * mm, "end": v(140.36, 35.11) * mm});
            skLineSegment(sketch, "E244", {"start": v(140.36, 35.11) * mm, "end": v(140.62, 33.56) * mm});
            skLineSegment(sketch, "E245", {"start": v(140.62, 33.56) * mm, "end": v(140.95, 32.06) * mm});
            skLineSegment(sketch, "E246", {"start": v(140.95, 32.06) * mm, "end": v(141.34, 30.61) * mm});
            skLineSegment(sketch, "E247", {"start": v(141.34, 30.61) * mm, "end": v(141.8, 29.22) * mm});
            skLineSegment(sketch, "E248", {"start": v(141.8, 29.22) * mm, "end": v(142.31, 27.88) * mm});
            skLineSegment(sketch, "E249", {"start": v(142.31, 27.88) * mm, "end": v(142.89, 26.6) * mm});
            skLineSegment(sketch, "E250", {"start": v(142.89, 26.6) * mm, "end": v(207.1, -88.47) * mm});
            skLineSegment(sketch, "E251", {"start": v(207.1, -88.47) * mm, "end": v(207.78, -89.99) * mm});
            skLineSegment(sketch, "E252", {"start": v(207.78, -89.99) * mm, "end": v(208.38, -91.58) * mm});
            skLineSegment(sketch, "E253", {"start": v(208.38, -91.58) * mm, "end": v(208.89, -93.25) * mm});
            skLineSegment(sketch, "E254", {"start": v(208.89, -93.25) * mm, "end": v(209.3, -95) * mm});
            skLineSegment(sketch, "E255", {"start": v(209.3, -95) * mm, "end": v(209.63, -96.83) * mm});
            skLineSegment(sketch, "E256", {"start": v(209.63, -96.83) * mm, "end": v(209.87, -98.74) * mm});
            skLineSegment(sketch, "E257", {"start": v(209.87, -98.74) * mm, "end": v(210.03, -100.72) * mm});
            skLineSegment(sketch, "E258", {"start": v(210.03, -100.72) * mm, "end": v(210.1, -102.77) * mm});
            skLineSegment(sketch, "E259", {"start": v(200.1, -102.84) * mm, "end": v(200.06, -101.63) * mm});
            skLineSegment(sketch, "E260", {"start": v(200.06, -101.63) * mm, "end": v(199.98, -100.39) * mm});
            skLineSegment(sketch, "E261", {"start": v(199.98, -100.39) * mm, "end": v(199.85, -99.13) * mm});
            skLineSegment(sketch, "E262", {"start": v(199.85, -99.13) * mm, "end": v(199.67, -97.88) * mm});
            skLineSegment(sketch, "E263", {"start": v(199.67, -97.88) * mm, "end": v(199.42, -96.64) * mm});
            skLineSegment(sketch, "E264", {"start": v(199.42, -96.64) * mm, "end": v(199.1, -95.42) * mm});
            skLineSegment(sketch, "E265", {"start": v(199.1, -95.42) * mm, "end": v(198.7, -94.24) * mm});
            skLineSegment(sketch, "E266", {"start": v(198.7, -94.24) * mm, "end": v(198.23, -93.12) * mm});
            skLineSegment(sketch, "E267", {"start": v(198.23, -93.12) * mm, "end": v(134, 22) * mm});
            skLineSegment(sketch, "E268", {"start": v(134, 22) * mm, "end": v(133.85, 22.3) * mm});
            skLineSegment(sketch, "E269", {"start": v(133.85, 22.3) * mm, "end": v(133.02, 24.17) * mm});
            skLineSegment(sketch, "E270", {"start": v(133.02, 24.17) * mm, "end": v(132.3, 26.06) * mm});
            skLineSegment(sketch, "E271", {"start": v(132.3, 26.06) * mm, "end": v(131.68, 28) * mm});
            skLineSegment(sketch, "E272", {"start": v(131.68, 28) * mm, "end": v(131.17, 29.94) * mm});
            skLineSegment(sketch, "E273", {"start": v(131.17, 29.94) * mm, "end": v(130.75, 31.92) * mm});
            skLineSegment(sketch, "E274", {"start": v(130.75, 31.92) * mm, "end": v(130.43, 33.92) * mm});
            skLineSegment(sketch, "E275", {"start": v(130.43, 33.92) * mm, "end": v(130.2, 35.94) * mm});
            skLineSegment(sketch, "E276", {"start": v(130.2, 35.94) * mm, "end": v(130.07, 37.98) * mm});
            skLineSegment(sketch, "E277", {"start": v(130.07, 37.98) * mm, "end": v(130.06, 38.2) * mm});
            skLineSegment(sketch, "E278", {"start": v(130.06, 38.2) * mm, "end": v(130.06, 53.7) * mm});
            skLineSegment(sketch, "E279", {"start": v(130.06, 53.7) * mm, "end": v(130.06, 53.8) * mm});
            skLineSegment(sketch, "E280", {"start": v(130.06, 53.8) * mm, "end": v(130.37, 57.06) * mm});
            skLineSegment(sketch, "E281", {"start": v(130.37, 57.06) * mm, "end": v(131.14, 60.11) * mm});
            skLineSegment(sketch, "E282", {"start": v(131.14, 60.11) * mm, "end": v(132.36, 62.89) * mm});
            skLineSegment(sketch, "E283", {"start": v(132.36, 62.89) * mm, "end": v(134.02, 65.3) * mm});
            skLineSegment(sketch, "E284", {"start": v(134.02, 65.3) * mm, "end": v(136.13, 67.3) * mm});
            skLineSegment(sketch, "E285", {"start": v(136.13, 67.3) * mm, "end": v(138.66, 68.8) * mm});
            skLineSegment(sketch, "E286", {"start": v(138.66, 68.8) * mm, "end": v(141.6, 69.74) * mm});
            skLineSegment(sketch, "E287", {"start": v(141.6, 69.74) * mm, "end": v(144.97, 70.03) * mm});
            skLineSegment(sketch, "E288", {"start": v(144.97, 70.03) * mm, "end": v(154.39, 70.03) * mm});
            skLineSegment(sketch, "E289", {"start": v(154.39, 70.03) * mm, "end": v(178.55, 70.03) * mm});
            skLineSegment(sketch, "E290", {"start": v(178.55, 70.03) * mm, "end": v(183.6, 70.55) * mm});
            skLineSegment(sketch, "E291", {"start": v(183.6, 70.55) * mm, "end": v(187.95, 71.95) * mm});
            skLineSegment(sketch, "E292", {"start": v(187.95, 71.95) * mm, "end": v(191.62, 74.22) * mm});
            skLineSegment(sketch, "E293", {"start": v(191.62, 74.22) * mm, "end": v(194.62, 77.34) * mm});
            skLineSegment(sketch, "E294", {"start": v(194.62, 77.34) * mm, "end": v(196.95, 81.3) * mm});
            skLineSegment(sketch, "E295", {"start": v(196.95, 81.3) * mm, "end": v(198.63, 86.09) * mm});
            skLineSegment(sketch, "E296", {"start": v(198.63, 86.09) * mm, "end": v(199.68, 91.68) * mm});
            skLineSegment(sketch, "E297", {"start": v(199.68, 91.68) * mm, "end": v(200.1, 98.07) * mm});
            skLineSegment(sketch, "E298", {"start": v(200.1, 98.07) * mm, "end": v(200.1, 320.41) * mm});
            skLineSegment(sketch, "E299", {"start": v(200.1, 320.41) * mm, "end": v(200.07, 320.63) * mm});
            skLineSegment(sketch, "E300", {"start": v(200.07, 320.63) * mm, "end": v(200, 320.83) * mm});
            skLineSegment(sketch, "E301", {"start": v(200, 320.83) * mm, "end": v(199.9, 321.01) * mm});
            skLineSegment(sketch, "E302", {"start": v(199.9, 321.01) * mm, "end": v(199.76, 321.18) * mm});
            skLineSegment(sketch, "E303", {"start": v(199.76, 321.18) * mm, "end": v(199.6, 321.31) * mm});
            skLineSegment(sketch, "E304", {"start": v(199.6, 321.31) * mm, "end": v(199.41, 321.42) * mm});
            skLineSegment(sketch, "E305", {"start": v(199.41, 321.42) * mm, "end": v(199.21, 321.48) * mm});
            skLineSegment(sketch, "E306", {"start": v(199.21, 321.48) * mm, "end": v(199, 321.5) * mm});
            skLineSegment(sketch, "E307", {"start": v(199, 321.5) * mm, "end": v(-199, 321.5) * mm});
            skLineSegment(sketch, "E308", {"start": v(-199, 321.5) * mm, "end": v(-199.21, 321.48) * mm});
            skLineSegment(sketch, "E309", {"start": v(-199.21, 321.48) * mm, "end": v(-199.41, 321.42) * mm});
            skLineSegment(sketch, "E310", {"start": v(-199.41, 321.42) * mm, "end": v(-199.6, 321.31) * mm});
            skLineSegment(sketch, "E311", {"start": v(-199.6, 321.31) * mm, "end": v(-199.76, 321.18) * mm});
            skLineSegment(sketch, "E312", {"start": v(-199.76, 321.18) * mm, "end": v(-199.9, 321.01) * mm});
            skLineSegment(sketch, "E313", {"start": v(-199.9, 321.01) * mm, "end": v(-200, 320.83) * mm});
            skLineSegment(sketch, "E314", {"start": v(-200, 320.83) * mm, "end": v(-200.07, 320.63) * mm});
            skLineSegment(sketch, "E315", {"start": v(-200.07, 320.63) * mm, "end": v(-200.1, 320.41) * mm});
            skLineSegment(sketch, "E316", {"start": v(-200.1, 320.41) * mm, "end": v(-200.1, 292.24) * mm});
            skLineSegment(sketch, "E317", {"start": v(-200.1, 292.24) * mm, "end": v(-200.1, 264.08) * mm});
            skLineSegment(sketch, "E318", {"start": v(-200.1, 264.08) * mm, "end": v(-200.11, 235.9) * mm});
            skLineSegment(sketch, "E319", {"start": v(-200.11, 235.9) * mm, "end": v(-200.12, 207.74) * mm});
            skLineSegment(sketch, "E320", {"start": v(-200.12, 207.74) * mm, "end": v(-200.13, 179.57) * mm});
            skLineSegment(sketch, "E321", {"start": v(-200.13, 179.57) * mm, "end": v(-200.13, 151.4) * mm});
            skLineSegment(sketch, "E322", {"start": v(-200.13, 151.4) * mm, "end": v(-200.13, 123.23) * mm});
            skLineSegment(sketch, "E323", {"start": v(-200.13, 123.23) * mm, "end": v(-200.11, 95.07) * mm});
            skLineSegment(sketch, "E324", {"start": v(-200.11, 95.07) * mm, "end": v(-199.9, 89.42) * mm});
            skLineSegment(sketch, "E325", {"start": v(-199.9, 89.42) * mm, "end": v(-199.18, 84.47) * mm});
            skLineSegment(sketch, "E326", {"start": v(-199.18, 84.47) * mm, "end": v(-197.94, 80.22) * mm});
            skLineSegment(sketch, "E327", {"start": v(-197.94, 80.22) * mm, "end": v(-196.18, 76.7) * mm});
            skLineSegment(sketch, "E328", {"start": v(-196.18, 76.7) * mm, "end": v(-193.9, 73.9) * mm});
            skLineSegment(sketch, "E329", {"start": v(-193.9, 73.9) * mm, "end": v(-191.07, 71.85) * mm});
            skLineSegment(sketch, "E330", {"start": v(-191.07, 71.85) * mm, "end": v(-187.7, 70.54) * mm});
            skLineSegment(sketch, "E331", {"start": v(-187.7, 70.54) * mm, "end": v(-183.78, 69.98) * mm});
            skLineSegment(sketch, "E332", {"start": v(-183.78, 69.98) * mm, "end": v(-154.39, 70.03) * mm});
            skLineSegment(sketch, "E333", {"start": v(-154.39, 70.03) * mm, "end": v(-144.97, 70.03) * mm});
            skLineSegment(sketch, "E334", {"start": v(-144.97, 70.03) * mm, "end": v(-141.6, 69.74) * mm});
            skLineSegment(sketch, "E335", {"start": v(-141.6, 69.74) * mm, "end": v(-138.66, 68.8) * mm});
            skLineSegment(sketch, "E336", {"start": v(-138.66, 68.8) * mm, "end": v(-136.13, 67.3) * mm});
            skLineSegment(sketch, "E337", {"start": v(-136.13, 67.3) * mm, "end": v(-134.02, 65.3) * mm});
            skLineSegment(sketch, "E338", {"start": v(-134.02, 65.3) * mm, "end": v(-132.36, 62.89) * mm});
            skLineSegment(sketch, "E339", {"start": v(-132.36, 62.89) * mm, "end": v(-131.14, 60.11) * mm});
            skLineSegment(sketch, "E340", {"start": v(-131.14, 60.11) * mm, "end": v(-130.37, 57.06) * mm});
            skLineSegment(sketch, "E341", {"start": v(-130.37, 57.06) * mm, "end": v(-130.06, 53.8) * mm});
            skLineSegment(sketch, "E342", {"start": v(-130.06, 53.8) * mm, "end": v(-130.06, 53.7) * mm});
            skLineSegment(sketch, "E343", {"start": v(-130.06, 53.7) * mm, "end": v(-130.06, 38.2) * mm});
            skLineSegment(sketch, "E344", {"start": v(-130.06, 38.2) * mm, "end": v(-130.07, 37.98) * mm});
            skLineSegment(sketch, "E345", {"start": v(-130.07, 37.98) * mm, "end": v(-130.2, 35.94) * mm});
            skLineSegment(sketch, "E346", {"start": v(-130.2, 35.94) * mm, "end": v(-130.43, 33.92) * mm});
            skLineSegment(sketch, "E347", {"start": v(-130.43, 33.92) * mm, "end": v(-130.75, 31.92) * mm});
            skLineSegment(sketch, "E348", {"start": v(-130.75, 31.92) * mm, "end": v(-131.17, 29.94) * mm});
            skLineSegment(sketch, "E349", {"start": v(-131.17, 29.94) * mm, "end": v(-131.68, 28) * mm});
            skLineSegment(sketch, "E350", {"start": v(-131.68, 28) * mm, "end": v(-132.3, 26.06) * mm});
            skLineSegment(sketch, "E351", {"start": v(-132.3, 26.06) * mm, "end": v(-133.02, 24.17) * mm});
            skLineSegment(sketch, "E352", {"start": v(-133.02, 24.17) * mm, "end": v(-133.85, 22.3) * mm});
            skLineSegment(sketch, "E353", {"start": v(-133.85, 22.3) * mm, "end": v(-134, 22) * mm});
            skLineSegment(sketch, "E354", {"start": v(-134, 22) * mm, "end": v(-198.23, -93.12) * mm});
            skLineSegment(sketch, "E355", {"start": v(-198.23, -93.12) * mm, "end": v(-198.7, -94.24) * mm});
            skLineSegment(sketch, "E356", {"start": v(-198.7, -94.24) * mm, "end": v(-199.1, -95.42) * mm});
            skLineSegment(sketch, "E357", {"start": v(-199.1, -95.42) * mm, "end": v(-199.42, -96.64) * mm});
            skLineSegment(sketch, "E358", {"start": v(-199.42, -96.64) * mm, "end": v(-199.67, -97.88) * mm});
            skLineSegment(sketch, "E359", {"start": v(-199.67, -97.88) * mm, "end": v(-199.85, -99.13) * mm});
            skLineSegment(sketch, "E360", {"start": v(-199.85, -99.13) * mm, "end": v(-199.98, -100.39) * mm});
            skLineSegment(sketch, "E361", {"start": v(-199.98, -100.39) * mm, "end": v(-200.06, -101.63) * mm});
            skLineSegment(sketch, "E362", {"start": v(-200.06, -101.63) * mm, "end": v(-200.1, -102.84) * mm});
            skLineSegment(sketch, "E363", {"start": v(-200.1, -102.84) * mm, "end": v(-200.1, -299.56) * mm});
            skLineSegment(sketch, "E364", {"start": v(-200.1, -299.56) * mm, "end": v(-198.87, -311.61) * mm});
            skLineSegment(sketch, "E365", {"start": v(-198.87, -311.61) * mm, "end": v(-195.35, -322.86) * mm});
            skLineSegment(sketch, "E366", {"start": v(-195.35, -322.86) * mm, "end": v(-189.8, -333.05) * mm});
            skLineSegment(sketch, "E367", {"start": v(-189.8, -333.05) * mm, "end": v(-182.45, -341.95) * mm});
            skLineSegment(sketch, "E368", {"start": v(-182.45, -341.95) * mm, "end": v(-173.56, -349.3) * mm});
            skLineSegment(sketch, "E369", {"start": v(-173.56, -349.3) * mm, "end": v(-163.37, -354.85) * mm});
            skLineSegment(sketch, "E370", {"start": v(-163.37, -354.85) * mm, "end": v(-152.12, -358.36) * mm});
            skLineSegment(sketch, "E371", {"start": v(-152.12, -358.36) * mm, "end": v(-140.07, -359.59) * mm});
            skLineSegment(sketch, "E372", {"start": v(-140.07, -359.59) * mm, "end": v(140.07, -359.59) * mm});
            skLineSegment(sketch, "E373", {"start": v(140.07, -359.59) * mm, "end": v(152.12, -358.36) * mm});
            skLineSegment(sketch, "E374", {"start": v(152.12, -358.36) * mm, "end": v(163.37, -354.85) * mm});
            skLineSegment(sketch, "E375", {"start": v(163.37, -354.85) * mm, "end": v(173.56, -349.3) * mm});
            skLineSegment(sketch, "E376", {"start": v(173.56, -349.3) * mm, "end": v(182.45, -341.95) * mm});
            skLineSegment(sketch, "E377", {"start": v(182.45, -341.95) * mm, "end": v(189.8, -333.05) * mm});
            skLineSegment(sketch, "E378", {"start": v(189.8, -333.05) * mm, "end": v(195.35, -322.86) * mm});
            skLineSegment(sketch, "E379", {"start": v(195.35, -322.86) * mm, "end": v(198.87, -311.61) * mm});
            skLineSegment(sketch, "E380", {"start": v(198.87, -311.61) * mm, "end": v(200.1, -299.56) * mm});
            skLineSegment(sketch, "E381", {"start": v(200.1, -299.56) * mm, "end": v(200.1, -102.84) * mm});
            skLineSegment(sketch, "E382", {"start": v(135.56, -62.93) * mm, "end": v(98.4, 3.64) * mm});
            skLineSegment(sketch, "E383", {"start": v(98.4, 3.64) * mm, "end": v(97.7, 5.11) * mm});
            skLineSegment(sketch, "E384", {"start": v(97.7, 5.11) * mm, "end": v(96.06, 8.82) * mm});
            skLineSegment(sketch, "E385", {"start": v(96.06, 8.82) * mm, "end": v(94.62, 12.6) * mm});
            skLineSegment(sketch, "E386", {"start": v(94.62, 12.6) * mm, "end": v(93.37, 16.42) * mm});
            skLineSegment(sketch, "E387", {"start": v(93.37, 16.42) * mm, "end": v(92.33, 20.3) * mm});
            skLineSegment(sketch, "E388", {"start": v(92.33, 20.3) * mm, "end": v(91.48, 24.24) * mm});
            skLineSegment(sketch, "E389", {"start": v(91.48, 24.24) * mm, "end": v(90.82, 28.2) * mm});
            skLineSegment(sketch, "E390", {"start": v(90.82, 28.2) * mm, "end": v(90.36, 32.22) * mm});
            skLineSegment(sketch, "E391", {"start": v(90.36, 32.22) * mm, "end": v(90.09, 36.27) * mm});
            skLineSegment(sketch, "E392", {"start": v(90.09, 36.27) * mm, "end": v(90.04, 37.34) * mm});
            skLineSegment(sketch, "E393", {"start": v(90.04, 37.34) * mm, "end": v(90.04, 54.12) * mm});
            skLineSegment(sketch, "E394", {"start": v(90.04, 54.12) * mm, "end": v(90.05, 66.3) * mm});
            skLineSegment(sketch, "E395", {"start": v(90.05, 66.3) * mm, "end": v(89.92, 68.88) * mm});
            skLineSegment(sketch, "E396", {"start": v(89.92, 68.88) * mm, "end": v(89.46, 71.2) * mm});
            skLineSegment(sketch, "E397", {"start": v(89.46, 71.2) * mm, "end": v(88.63, 73.24) * mm});
            skLineSegment(sketch, "E398", {"start": v(88.63, 73.24) * mm, "end": v(87.4, 74.97) * mm});
            skLineSegment(sketch, "E399", {"start": v(87.4, 74.97) * mm, "end": v(85.74, 76.35) * mm});
            skLineSegment(sketch, "E400", {"start": v(85.74, 76.35) * mm, "end": v(83.59, 77.37) * mm});
            skLineSegment(sketch, "E401", {"start": v(83.59, 77.37) * mm, "end": v(80.92, 77.98) * mm});
            skLineSegment(sketch, "E402", {"start": v(80.92, 77.98) * mm, "end": v(77.7, 78.16) * mm});
            skLineSegment(sketch, "E403", {"start": v(77.7, 78.16) * mm, "end": v(-78.48, 78.16) * mm});
            skLineSegment(sketch, "E404", {"start": v(-78.48, 78.16) * mm, "end": v(-81.67, 77.95) * mm});
            skLineSegment(sketch, "E405", {"start": v(-81.67, 77.95) * mm, "end": v(-84.26, 77.31) * mm});
            skLineSegment(sketch, "E406", {"start": v(-84.26, 77.31) * mm, "end": v(-86.28, 76.27) * mm});
            skLineSegment(sketch, "E407", {"start": v(-86.28, 76.27) * mm, "end": v(-87.8, 74.82) * mm});
            skLineSegment(sketch, "E408", {"start": v(-87.8, 74.82) * mm, "end": v(-88.88, 72.99) * mm});
            skLineSegment(sketch, "E409", {"start": v(-88.88, 72.99) * mm, "end": v(-89.58, 70.77) * mm});
            skLineSegment(sketch, "E410", {"start": v(-89.58, 70.77) * mm, "end": v(-89.96, 68.19) * mm});
            skLineSegment(sketch, "E411", {"start": v(-89.96, 68.19) * mm, "end": v(-90.06, 65.24) * mm});
            skLineSegment(sketch, "E412", {"start": v(-90.06, 65.24) * mm, "end": v(-90.04, 54.12) * mm});
            skLineSegment(sketch, "E413", {"start": v(-90.04, 54.12) * mm, "end": v(-90.04, 37.34) * mm});
            skLineSegment(sketch, "E414", {"start": v(-90.04, 37.34) * mm, "end": v(-90.09, 36.27) * mm});
            skLineSegment(sketch, "E415", {"start": v(-90.09, 36.27) * mm, "end": v(-90.36, 32.22) * mm});
            skLineSegment(sketch, "E416", {"start": v(-90.36, 32.22) * mm, "end": v(-90.82, 28.2) * mm});
            skLineSegment(sketch, "E417", {"start": v(-90.82, 28.2) * mm, "end": v(-91.48, 24.24) * mm});
            skLineSegment(sketch, "E418", {"start": v(-91.48, 24.24) * mm, "end": v(-92.33, 20.3) * mm});
            skLineSegment(sketch, "E419", {"start": v(-92.33, 20.3) * mm, "end": v(-93.37, 16.42) * mm});
            skLineSegment(sketch, "E420", {"start": v(-93.37, 16.42) * mm, "end": v(-94.62, 12.6) * mm});
            skLineSegment(sketch, "E421", {"start": v(-94.62, 12.6) * mm, "end": v(-96.06, 8.82) * mm});
            skLineSegment(sketch, "E422", {"start": v(-96.06, 8.82) * mm, "end": v(-97.7, 5.11) * mm});
            skLineSegment(sketch, "E423", {"start": v(-97.7, 5.11) * mm, "end": v(-98.4, 3.64) * mm});
            skLineSegment(sketch, "E424", {"start": v(-98.4, 3.64) * mm, "end": v(-139.65, -70.26) * mm});
            skLineSegment(sketch, "E425", {"start": v(-139.65, -70.26) * mm, "end": v(-145.43, -80.41) * mm});
            skLineSegment(sketch, "E426", {"start": v(-145.43, -80.41) * mm, "end": v(-150.05, -88.41) * mm});
            skLineSegment(sketch, "E427", {"start": v(-150.05, -88.41) * mm, "end": v(-153.62, -95.08) * mm});
            skLineSegment(sketch, "E428", {"start": v(-153.62, -95.08) * mm, "end": v(-156.27, -101.22) * mm});
            skLineSegment(sketch, "E429", {"start": v(-156.27, -101.22) * mm, "end": v(-158.12, -107.64) * mm});
            skLineSegment(sketch, "E430", {"start": v(-158.12, -107.64) * mm, "end": v(-159.29, -115.16) * mm});
            skLineSegment(sketch, "E431", {"start": v(-159.29, -115.16) * mm, "end": v(-159.9, -124.59) * mm});
            skLineSegment(sketch, "E432", {"start": v(-159.9, -124.59) * mm, "end": v(-160.08, -136.73) * mm});
            skLineSegment(sketch, "E433", {"start": v(-160.08, -136.73) * mm, "end": v(-160.08, -317.56) * mm});
            skLineSegment(sketch, "E434", {"start": v(-160.08, -317.56) * mm, "end": v(-159.66, -321.55) * mm});
            skLineSegment(sketch, "E435", {"start": v(-159.66, -321.55) * mm, "end": v(-158.48, -325.29) * mm});
            skLineSegment(sketch, "E436", {"start": v(-158.48, -325.29) * mm, "end": v(-156.62, -328.69) * mm});
            skLineSegment(sketch, "E437", {"start": v(-156.62, -328.69) * mm, "end": v(-154.16, -331.66) * mm});
            skLineSegment(sketch, "E438", {"start": v(-154.16, -331.66) * mm, "end": v(-151.19, -334.12) * mm});
            skLineSegment(sketch, "E439", {"start": v(-151.19, -334.12) * mm, "end": v(-147.8, -335.98) * mm});
            skLineSegment(sketch, "E440", {"start": v(-147.8, -335.98) * mm, "end": v(-144.06, -337.16) * mm});
            skLineSegment(sketch, "E441", {"start": v(-144.06, -337.16) * mm, "end": v(-140.07, -337.57) * mm});
            skLineSegment(sketch, "E442", {"start": v(-140.07, -337.57) * mm, "end": v(140.07, -337.57) * mm});
            skLineSegment(sketch, "E443", {"start": v(140.07, -337.57) * mm, "end": v(144.06, -337.16) * mm});
            skLineSegment(sketch, "E444", {"start": v(144.06, -337.16) * mm, "end": v(147.8, -335.98) * mm});
            skLineSegment(sketch, "E445", {"start": v(147.8, -335.98) * mm, "end": v(151.19, -334.12) * mm});
            skLineSegment(sketch, "E446", {"start": v(151.19, -334.12) * mm, "end": v(154.16, -331.66) * mm});
            skLineSegment(sketch, "E447", {"start": v(154.16, -331.66) * mm, "end": v(156.62, -328.69) * mm});
            skLineSegment(sketch, "E448", {"start": v(156.62, -328.69) * mm, "end": v(158.48, -325.29) * mm});
            skLineSegment(sketch, "E449", {"start": v(158.48, -325.29) * mm, "end": v(159.66, -321.55) * mm});
            skLineSegment(sketch, "E450", {"start": v(159.66, -321.55) * mm, "end": v(160.08, -317.56) * mm});
            skLineSegment(sketch, "E451", {"start": v(160.08, -317.56) * mm, "end": v(160.08, -143.43) * mm});
            skLineSegment(sketch, "E452", {"start": v(160.08, -143.43) * mm, "end": v(159.93, -128.53) * mm});
            skLineSegment(sketch, "E453", {"start": v(159.93, -128.53) * mm, "end": v(159.37, -117.25) * mm});
            skLineSegment(sketch, "E454", {"start": v(159.37, -117.25) * mm, "end": v(158.18, -108.46) * mm});
            skLineSegment(sketch, "E455", {"start": v(158.18, -108.46) * mm, "end": v(156.16, -101.06) * mm});
            skLineSegment(sketch, "E456", {"start": v(156.16, -101.06) * mm, "end": v(153.1, -93.92) * mm});
            skLineSegment(sketch, "E457", {"start": v(153.1, -93.92) * mm, "end": v(148.77, -85.93) * mm});
            skLineSegment(sketch, "E458", {"start": v(148.77, -85.93) * mm, "end": v(143, -75.97) * mm});
            skLineSegment(sketch, "E459", {"start": v(143, -75.97) * mm, "end": v(135.56, -62.93) * mm});
            skLineSegment(sketch, "E460", {"start": v(79.93, 68.01) * mm, "end": v(79.38, 68.1) * mm});
            skLineSegment(sketch, "E461", {"start": v(79.38, 68.1) * mm, "end": v(78.8, 68.14) * mm});
            skLineSegment(sketch, "E462", {"start": v(78.8, 68.14) * mm, "end": v(78.25, 68.16) * mm});
            skLineSegment(sketch, "E463", {"start": v(78.25, 68.16) * mm, "end": v(77.82, 68.16) * mm});
            skLineSegment(sketch, "E464", {"start": v(77.82, 68.16) * mm, "end": v(77.76, 68.16) * mm});
            skLineSegment(sketch, "E465", {"start": v(-78.48, 68.15) * mm, "end": v(-79.92, 68.1) * mm});
            skLineSegment(sketch, "E466", {"start": v(-79.92, 68.1) * mm, "end": v(-80, 67.33) * mm});
            skLineSegment(sketch, "E467", {"start": v(-80, 67.33) * mm, "end": v(-80.04, 66.55) * mm});
            skLineSegment(sketch, "E468", {"start": v(-80.04, 66.55) * mm, "end": v(-80.06, 65.83) * mm});
            skLineSegment(sketch, "E469", {"start": v(-80.06, 65.83) * mm, "end": v(-80.06, 65.26) * mm});
            skLineSegment(sketch, "E470", {"start": v(-80.06, 65.26) * mm, "end": v(-80.04, 54.12) * mm});
            skLineSegment(sketch, "E471", {"start": v(-80.04, 54.12) * mm, "end": v(-80.04, 37.12) * mm});
            skLineSegment(sketch, "E472", {"start": v(-80.04, 37.12) * mm, "end": v(-80.1, 35.84) * mm});
            skLineSegment(sketch, "E473", {"start": v(-80.1, 35.84) * mm, "end": v(-80.4, 31.3) * mm});
            skLineSegment(sketch, "E474", {"start": v(-80.4, 31.3) * mm, "end": v(-80.92, 26.78) * mm});
            skLineSegment(sketch, "E475", {"start": v(-80.92, 26.78) * mm, "end": v(-81.66, 22.31) * mm});
            skLineSegment(sketch, "E476", {"start": v(-81.66, 22.31) * mm, "end": v(-82.62, 17.9) * mm});
            skLineSegment(sketch, "E477", {"start": v(-82.62, 17.9) * mm, "end": v(-83.8, 13.53) * mm});
            skLineSegment(sketch, "E478", {"start": v(-83.8, 13.53) * mm, "end": v(-85.2, 9.22) * mm});
            skLineSegment(sketch, "E479", {"start": v(-85.2, 9.22) * mm, "end": v(-86.82, 4.98) * mm});
            skLineSegment(sketch, "E480", {"start": v(-86.82, 4.98) * mm, "end": v(-88.67, 0.82) * mm});
            skLineSegment(sketch, "E481", {"start": v(-88.67, 0.82) * mm, "end": v(-89.51, -0.95) * mm});
            skLineSegment(sketch, "E482", {"start": v(-89.51, -0.95) * mm, "end": v(-89.67, -1.24) * mm});
            skLineSegment(sketch, "E483", {"start": v(-130.91, -75.14) * mm, "end": v(-132.2, -77.43) * mm});
            skLineSegment(sketch, "E484", {"start": v(-132.2, -77.43) * mm, "end": v(-133.5, -79.71) * mm});
            skLineSegment(sketch, "E485", {"start": v(-133.5, -79.71) * mm, "end": v(-134.8, -81.99) * mm});
            skLineSegment(sketch, "E486", {"start": v(-134.8, -81.99) * mm, "end": v(-136.12, -84.26) * mm});
            skLineSegment(sketch, "E487", {"start": v(-136.12, -84.26) * mm, "end": v(-137.44, -86.53) * mm});
            skLineSegment(sketch, "E488", {"start": v(-137.44, -86.53) * mm, "end": v(-138.75, -88.8) * mm});
            skLineSegment(sketch, "E489", {"start": v(-138.75, -88.8) * mm, "end": v(-140.06, -91.08) * mm});
            skLineSegment(sketch, "E490", {"start": v(-140.06, -91.08) * mm, "end": v(-141.36, -93.36) * mm});
            skLineSegment(sketch, "E491", {"start": v(-141.36, -93.36) * mm, "end": v(-142.13, -94.73) * mm});
            skLineSegment(sketch, "E492", {"start": v(-142.13, -94.73) * mm, "end": v(-142.89, -96.1) * mm});
            skLineSegment(sketch, "E493", {"start": v(-142.89, -96.1) * mm, "end": v(-143.63, -97.5) * mm});
            skLineSegment(sketch, "E494", {"start": v(-143.63, -97.5) * mm, "end": v(-144.35, -98.9) * mm});
            skLineSegment(sketch, "E495", {"start": v(-144.35, -98.9) * mm, "end": v(-145.05, -100.31) * mm});
            skLineSegment(sketch, "E496", {"start": v(-145.05, -100.31) * mm, "end": v(-145.7, -101.75) * mm});
            skLineSegment(sketch, "E497", {"start": v(-145.7, -101.75) * mm, "end": v(-146.32, -103.2) * mm});
            skLineSegment(sketch, "E498", {"start": v(-146.32, -103.2) * mm, "end": v(-146.88, -104.66) * mm});
            skLineSegment(sketch, "E499", {"start": v(-146.88, -104.66) * mm, "end": v(-147.99, -108.32) * mm});
            skLineSegment(sketch, "E500", {"start": v(-147.99, -108.32) * mm, "end": v(-148.8, -112.24) * mm});
            skLineSegment(sketch, "E501", {"start": v(-148.8, -112.24) * mm, "end": v(-149.37, -116.33) * mm});
            skLineSegment(sketch, "E502", {"start": v(-149.37, -116.33) * mm, "end": v(-149.74, -120.52) * mm});
            skLineSegment(sketch, "E503", {"start": v(-149.74, -120.52) * mm, "end": v(-149.95, -124.74) * mm});
            skLineSegment(sketch, "E504", {"start": v(-149.95, -124.74) * mm, "end": v(-150.05, -128.9) * mm});
            skLineSegment(sketch, "E505", {"start": v(-150.05, -128.9) * mm, "end": v(-150.07, -132.92) * mm});
            skLineSegment(sketch, "E506", {"start": v(-150.07, -132.92) * mm, "end": v(-150.07, -136.73) * mm});
            skLineSegment(sketch, "E507", {"start": v(-150.07, -317.56) * mm, "end": v(-149.86, -319.54) * mm});
            skLineSegment(sketch, "E508", {"start": v(-149.86, -319.54) * mm, "end": v(-149.26, -321.4) * mm});
            skLineSegment(sketch, "E509", {"start": v(-149.26, -321.4) * mm, "end": v(-148.32, -323.1) * mm});
            skLineSegment(sketch, "E510", {"start": v(-148.32, -323.1) * mm, "end": v(-147.09, -324.58) * mm});
            skLineSegment(sketch, "E511", {"start": v(-147.09, -324.58) * mm, "end": v(-145.6, -325.82) * mm});
            skLineSegment(sketch, "E512", {"start": v(-145.6, -325.82) * mm, "end": v(-143.9, -326.76) * mm});
            skLineSegment(sketch, "E513", {"start": v(-143.9, -326.76) * mm, "end": v(-142.04, -327.36) * mm});
            skLineSegment(sketch, "E514", {"start": v(-142.04, -327.36) * mm, "end": v(-140.07, -327.57) * mm});
            skLineSegment(sketch, "E515", {"start": v(140.07, -327.57) * mm, "end": v(142.04, -327.36) * mm});
            skLineSegment(sketch, "E516", {"start": v(142.04, -327.36) * mm, "end": v(143.9, -326.76) * mm});
            skLineSegment(sketch, "E517", {"start": v(143.9, -326.76) * mm, "end": v(145.6, -325.82) * mm});
            skLineSegment(sketch, "E518", {"start": v(145.6, -325.82) * mm, "end": v(147.09, -324.58) * mm});
            skLineSegment(sketch, "E519", {"start": v(147.09, -324.58) * mm, "end": v(148.32, -323.1) * mm});
            skLineSegment(sketch, "E520", {"start": v(148.32, -323.1) * mm, "end": v(149.26, -321.4) * mm});
            skLineSegment(sketch, "E521", {"start": v(149.26, -321.4) * mm, "end": v(149.86, -319.54) * mm});
            skLineSegment(sketch, "E522", {"start": v(149.86, -319.54) * mm, "end": v(150.07, -317.56) * mm});
            skLineSegment(sketch, "E523", {"start": v(150.07, -143.43) * mm, "end": v(150.09, -138.97) * mm});
            skLineSegment(sketch, "E524", {"start": v(150.09, -138.97) * mm, "end": v(150.1, -134.16) * mm});
            skLineSegment(sketch, "E525", {"start": v(150.1, -134.16) * mm, "end": v(150.04, -129.1) * mm});
            skLineSegment(sketch, "E526", {"start": v(150.04, -129.1) * mm, "end": v(149.86, -123.95) * mm});
            skLineSegment(sketch, "E527", {"start": v(149.86, -123.95) * mm, "end": v(149.52, -118.82) * mm});
            skLineSegment(sketch, "E528", {"start": v(149.52, -118.82) * mm, "end": v(148.94, -113.84) * mm});
            skLineSegment(sketch, "E529", {"start": v(148.94, -113.84) * mm, "end": v(148.08, -109.14) * mm});
            skLineSegment(sketch, "E530", {"start": v(148.08, -109.14) * mm, "end": v(146.88, -104.84) * mm});
            skLineSegment(sketch, "E531", {"start": v(146.88, -104.84) * mm, "end": v(146.23, -103.07) * mm});
            skLineSegment(sketch, "E532", {"start": v(146.23, -103.07) * mm, "end": v(145.51, -101.32) * mm});
            skLineSegment(sketch, "E533", {"start": v(145.51, -101.32) * mm, "end": v(144.73, -99.59) * mm});
            skLineSegment(sketch, "E534", {"start": v(144.73, -99.59) * mm, "end": v(143.9, -97.87) * mm});
            skLineSegment(sketch, "E535", {"start": v(143.9, -97.87) * mm, "end": v(143.02, -96.18) * mm});
            skLineSegment(sketch, "E536", {"start": v(143.02, -96.18) * mm, "end": v(142.12, -94.5) * mm});
            skLineSegment(sketch, "E537", {"start": v(142.12, -94.5) * mm, "end": v(141.2, -92.85) * mm});
            skLineSegment(sketch, "E538", {"start": v(141.2, -92.85) * mm, "end": v(140.27, -91.2) * mm});
            skLineSegment(sketch, "E539", {"start": v(140.27, -91.2) * mm, "end": v(138.6, -88.28) * mm});
            skLineSegment(sketch, "E540", {"start": v(138.6, -88.28) * mm, "end": v(136.9, -85.36) * mm});
            skLineSegment(sketch, "E541", {"start": v(136.9, -85.36) * mm, "end": v(135.21, -82.44) * mm});
            skLineSegment(sketch, "E542", {"start": v(135.21, -82.44) * mm, "end": v(133.52, -79.52) * mm});
            skLineSegment(sketch, "E543", {"start": v(133.52, -79.52) * mm, "end": v(131.83, -76.6) * mm});
            skLineSegment(sketch, "E544", {"start": v(131.83, -76.6) * mm, "end": v(130.15, -73.68) * mm});
            skLineSegment(sketch, "E545", {"start": v(130.15, -73.68) * mm, "end": v(128.47, -70.75) * mm});
            skLineSegment(sketch, "E546", {"start": v(128.47, -70.75) * mm, "end": v(126.82, -67.8) * mm});
            skLineSegment(sketch, "E547", {"start": v(89.51, -0.95) * mm, "end": v(88.67, 0.82) * mm});
            skLineSegment(sketch, "E548", {"start": v(88.67, 0.82) * mm, "end": v(86.82, 4.98) * mm});
            skLineSegment(sketch, "E549", {"start": v(86.82, 4.98) * mm, "end": v(85.2, 9.22) * mm});
            skLineSegment(sketch, "E550", {"start": v(85.2, 9.22) * mm, "end": v(83.8, 13.53) * mm});
            skLineSegment(sketch, "E551", {"start": v(83.8, 13.53) * mm, "end": v(82.62, 17.9) * mm});
            skLineSegment(sketch, "E552", {"start": v(82.62, 17.9) * mm, "end": v(81.66, 22.31) * mm});
            skLineSegment(sketch, "E553", {"start": v(81.66, 22.31) * mm, "end": v(80.92, 26.78) * mm});
            skLineSegment(sketch, "E554", {"start": v(80.92, 26.78) * mm, "end": v(80.4, 31.3) * mm});
            skLineSegment(sketch, "E555", {"start": v(80.4, 31.3) * mm, "end": v(80.1, 35.84) * mm});
            skLineSegment(sketch, "E556", {"start": v(80.1, 35.84) * mm, "end": v(80.04, 37.12) * mm});
            skLineSegment(sketch, "E557", {"start": v(80.04, 37.12) * mm, "end": v(80.04, 54.13) * mm});
            skLineSegment(sketch, "E558", {"start": v(80.04, 54.13) * mm, "end": v(80.04, 66.3) * mm});
            skLineSegment(sketch, "E559", {"start": v(80.04, 66.3) * mm, "end": v(80.04, 66.66) * mm});
            skLineSegment(sketch, "E560", {"start": v(80.04, 66.66) * mm, "end": v(80.02, 67.1) * mm});
            skLineSegment(sketch, "E561", {"start": v(80.02, 67.1) * mm, "end": v(79.99, 67.56) * mm});
            skLineSegment(sketch, "E562", {"start": v(79.99, 67.56) * mm, "end": v(79.93, 68.01) * mm});
            skSolve(sketch);
        }
        {
            var Q0;
            Q0=makeQuery(id+"F12.imprint","IMPRINT",FACE,{"disambiguationData":[TD([[makeQuery(id+"F12.imprint","IMPRINT",EDGE,{"derivedFrom":sQuery(id+"F12.wireOp",EDGE,"E259")}),1.0]])]});
            extrude(context, id + "F13", {"entities" : qUnion([Q0]), "depth" : 20 * mm, "offsetDistance" : 25 * mm});
        }
        {
            var Q0;
            Q0=makeQuery(id+"F13.opExtrude","SWEPT_BODY",BODY,{"disambiguationData":[OSD([sQuery(id+"F12.wireOp",EDGE,"E259"),sQuery(id+"F12.wireOp",EDGE,"E260"),sQuery(id+"F12.wireOp",EDGE,"E261"),sQuery(id+"F12.wireOp",EDGE,"E262"),sQuery(id+"F12.wireOp",EDGE,"E263"),sQuery(id+"F12.wireOp",EDGE,"E264"),sQuery(id+"F12.wireOp",EDGE,"E265"),sQuery(id+"F12.wireOp",EDGE,"E266"),sQuery(id+"F12.wireOp",EDGE,"E267"),sQuery(id+"F12.wireOp",EDGE,"E268"),sQuery(id+"F12.wireOp",EDGE,"E269"),sQuery(id+"F12.wireOp",EDGE,"E270"),sQuery(id+"F12.wireOp",EDGE,"E271"),sQuery(id+"F12.wireOp",EDGE,"E272"),sQuery(id+"F12.wireOp",EDGE,"E273"),sQuery(id+"F12.wireOp",EDGE,"E274"),sQuery(id+"F12.wireOp",EDGE,"E275"),sQuery(id+"F12.wireOp",EDGE,"E276"),sQuery(id+"F12.wireOp",EDGE,"E277"),sQuery(id+"F12.wireOp",EDGE,"E278"),sQuery(id+"F12.wireOp",EDGE,"E279"),sQuery(id+"F12.wireOp",EDGE,"E280"),sQuery(id+"F12.wireOp",EDGE,"E281"),sQuery(id+"F12.wireOp",EDGE,"E282"),sQuery(id+"F12.wireOp",EDGE,"E283"),sQuery(id+"F12.wireOp",EDGE,"E284"),sQuery(id+"F12.wireOp",EDGE,"E285"),sQuery(id+"F12.wireOp",EDGE,"E286"),sQuery(id+"F12.wireOp",EDGE,"E287"),sQuery(id+"F12.wireOp",EDGE,"E288"),sQuery(id+"F12.wireOp",EDGE,"E289"),sQuery(id+"F12.wireOp",EDGE,"E290"),sQuery(id+"F12.wireOp",EDGE,"E291"),sQuery(id+"F12.wireOp",EDGE,"E292"),sQuery(id+"F12.wireOp",EDGE,"E293"),sQuery(id+"F12.wireOp",EDGE,"E294"),sQuery(id+"F12.wireOp",EDGE,"E295"),sQuery(id+"F12.wireOp",EDGE,"E296"),sQuery(id+"F12.wireOp",EDGE,"E297"),sQuery(id+"F12.wireOp",EDGE,"E298"),sQuery(id+"F12.wireOp",EDGE,"E299"),sQuery(id+"F12.wireOp",EDGE,"E300"),sQuery(id+"F12.wireOp",EDGE,"E301"),sQuery(id+"F12.wireOp",EDGE,"E302"),sQuery(id+"F12.wireOp",EDGE,"E303"),sQuery(id+"F12.wireOp",EDGE,"E304"),sQuery(id+"F12.wireOp",EDGE,"E305"),sQuery(id+"F12.wireOp",EDGE,"E306"),sQuery(id+"F12.wireOp",EDGE,"E307"),sQuery(id+"F12.wireOp",EDGE,"E308"),sQuery(id+"F12.wireOp",EDGE,"E309"),sQuery(id+"F12.wireOp",EDGE,"E310"),sQuery(id+"F12.wireOp",EDGE,"E311"),sQuery(id+"F12.wireOp",EDGE,"E312"),sQuery(id+"F12.wireOp",EDGE,"E313"),sQuery(id+"F12.wireOp",EDGE,"E314"),sQuery(id+"F12.wireOp",EDGE,"E315"),sQuery(id+"F12.wireOp",EDGE,"E316"),sQuery(id+"F12.wireOp",EDGE,"E317"),sQuery(id+"F12.wireOp",EDGE,"E318"),sQuery(id+"F12.wireOp",EDGE,"E319"),sQuery(id+"F12.wireOp",EDGE,"E320"),sQuery(id+"F12.wireOp",EDGE,"E321"),sQuery(id+"F12.wireOp",EDGE,"E322"),sQuery(id+"F12.wireOp",EDGE,"E323"),sQuery(id+"F12.wireOp",EDGE,"E324"),sQuery(id+"F12.wireOp",EDGE,"E325"),sQuery(id+"F12.wireOp",EDGE,"E326"),sQuery(id+"F12.wireOp",EDGE,"E327"),sQuery(id+"F12.wireOp",EDGE,"E328"),sQuery(id+"F12.wireOp",EDGE,"E329"),sQuery(id+"F12.wireOp",EDGE,"E330"),sQuery(id+"F12.wireOp",EDGE,"E331"),sQuery(id+"F12.wireOp",EDGE,"E332"),sQuery(id+"F12.wireOp",EDGE,"E333"),sQuery(id+"F12.wireOp",EDGE,"E334"),sQuery(id+"F12.wireOp",EDGE,"E335"),sQuery(id+"F12.wireOp",EDGE,"E336"),sQuery(id+"F12.wireOp",EDGE,"E337"),sQuery(id+"F12.wireOp",EDGE,"E338"),sQuery(id+"F12.wireOp",EDGE,"E339"),sQuery(id+"F12.wireOp",EDGE,"E340"),sQuery(id+"F12.wireOp",EDGE,"E341"),sQuery(id+"F12.wireOp",EDGE,"E342"),sQuery(id+"F12.wireOp",EDGE,"E343"),sQuery(id+"F12.wireOp",EDGE,"E344"),sQuery(id+"F12.wireOp",EDGE,"E345"),sQuery(id+"F12.wireOp",EDGE,"E346"),sQuery(id+"F12.wireOp",EDGE,"E347"),sQuery(id+"F12.wireOp",EDGE,"E348"),sQuery(id+"F12.wireOp",EDGE,"E349"),sQuery(id+"F12.wireOp",EDGE,"E350"),sQuery(id+"F12.wireOp",EDGE,"E351"),sQuery(id+"F12.wireOp",EDGE,"E352"),sQuery(id+"F12.wireOp",EDGE,"E353"),sQuery(id+"F12.wireOp",EDGE,"E354"),sQuery(id+"F12.wireOp",EDGE,"E355"),sQuery(id+"F12.wireOp",EDGE,"E356"),sQuery(id+"F12.wireOp",EDGE,"E357"),sQuery(id+"F12.wireOp",EDGE,"E358"),sQuery(id+"F12.wireOp",EDGE,"E359"),sQuery(id+"F12.wireOp",EDGE,"E360"),sQuery(id+"F12.wireOp",EDGE,"E361"),sQuery(id+"F12.wireOp",EDGE,"E362"),sQuery(id+"F12.wireOp",EDGE,"E363"),sQuery(id+"F12.wireOp",EDGE,"E364"),sQuery(id+"F12.wireOp",EDGE,"E365"),sQuery(id+"F12.wireOp",EDGE,"E366"),sQuery(id+"F12.wireOp",EDGE,"E367"),sQuery(id+"F12.wireOp",EDGE,"E368"),sQuery(id+"F12.wireOp",EDGE,"E369"),sQuery(id+"F12.wireOp",EDGE,"E370"),sQuery(id+"F12.wireOp",EDGE,"E371"),sQuery(id+"F12.wireOp",EDGE,"E372"),sQuery(id+"F12.wireOp",EDGE,"E373"),sQuery(id+"F12.wireOp",EDGE,"E374"),sQuery(id+"F12.wireOp",EDGE,"E375"),sQuery(id+"F12.wireOp",EDGE,"E376"),sQuery(id+"F12.wireOp",EDGE,"E377"),sQuery(id+"F12.wireOp",EDGE,"E378"),sQuery(id+"F12.wireOp",EDGE,"E379"),sQuery(id+"F12.wireOp",EDGE,"E380"),sQuery(id+"F12.wireOp",EDGE,"E381"),sQuery(id+"F12.wireOp",EDGE,"E382"),sQuery(id+"F12.wireOp",EDGE,"E383"),sQuery(id+"F12.wireOp",EDGE,"E384"),sQuery(id+"F12.wireOp",EDGE,"E385"),sQuery(id+"F12.wireOp",EDGE,"E386"),sQuery(id+"F12.wireOp",EDGE,"E387"),sQuery(id+"F12.wireOp",EDGE,"E388"),sQuery(id+"F12.wireOp",EDGE,"E389"),sQuery(id+"F12.wireOp",EDGE,"E390"),sQuery(id+"F12.wireOp",EDGE,"E391"),sQuery(id+"F12.wireOp",EDGE,"E392"),sQuery(id+"F12.wireOp",EDGE,"E393"),sQuery(id+"F12.wireOp",EDGE,"E394"),sQuery(id+"F12.wireOp",EDGE,"E395"),sQuery(id+"F12.wireOp",EDGE,"E396"),sQuery(id+"F12.wireOp",EDGE,"E397"),sQuery(id+"F12.wireOp",EDGE,"E398"),sQuery(id+"F12.wireOp",EDGE,"E399"),sQuery(id+"F12.wireOp",EDGE,"E400"),sQuery(id+"F12.wireOp",EDGE,"E401"),sQuery(id+"F12.wireOp",EDGE,"E402"),sQuery(id+"F12.wireOp",EDGE,"E403"),sQuery(id+"F12.wireOp",EDGE,"E404"),sQuery(id+"F12.wireOp",EDGE,"E405"),sQuery(id+"F12.wireOp",EDGE,"E406"),sQuery(id+"F12.wireOp",EDGE,"E407"),sQuery(id+"F12.wireOp",EDGE,"E408"),sQuery(id+"F12.wireOp",EDGE,"E409"),sQuery(id+"F12.wireOp",EDGE,"E410"),sQuery(id+"F12.wireOp",EDGE,"E411"),sQuery(id+"F12.wireOp",EDGE,"E412"),sQuery(id+"F12.wireOp",EDGE,"E413"),sQuery(id+"F12.wireOp",EDGE,"E414"),sQuery(id+"F12.wireOp",EDGE,"E415"),sQuery(id+"F12.wireOp",EDGE,"E416"),sQuery(id+"F12.wireOp",EDGE,"E417"),sQuery(id+"F12.wireOp",EDGE,"E418"),sQuery(id+"F12.wireOp",EDGE,"E419"),sQuery(id+"F12.wireOp",EDGE,"E420"),sQuery(id+"F12.wireOp",EDGE,"E421"),sQuery(id+"F12.wireOp",EDGE,"E422"),sQuery(id+"F12.wireOp",EDGE,"E423"),sQuery(id+"F12.wireOp",EDGE,"E424"),sQuery(id+"F12.wireOp",EDGE,"E425"),sQuery(id+"F12.wireOp",EDGE,"E426"),sQuery(id+"F12.wireOp",EDGE,"E427"),sQuery(id+"F12.wireOp",EDGE,"E428"),sQuery(id+"F12.wireOp",EDGE,"E429"),sQuery(id+"F12.wireOp",EDGE,"E430"),sQuery(id+"F12.wireOp",EDGE,"E431"),sQuery(id+"F12.wireOp",EDGE,"E432"),sQuery(id+"F12.wireOp",EDGE,"E433"),sQuery(id+"F12.wireOp",EDGE,"E434"),sQuery(id+"F12.wireOp",EDGE,"E435"),sQuery(id+"F12.wireOp",EDGE,"E436"),sQuery(id+"F12.wireOp",EDGE,"E437"),sQuery(id+"F12.wireOp",EDGE,"E438"),sQuery(id+"F12.wireOp",EDGE,"E439"),sQuery(id+"F12.wireOp",EDGE,"E440"),sQuery(id+"F12.wireOp",EDGE,"E441"),sQuery(id+"F12.wireOp",EDGE,"E442"),sQuery(id+"F12.wireOp",EDGE,"E443"),sQuery(id+"F12.wireOp",EDGE,"E444"),sQuery(id+"F12.wireOp",EDGE,"E445"),sQuery(id+"F12.wireOp",EDGE,"E446"),sQuery(id+"F12.wireOp",EDGE,"E447"),sQuery(id+"F12.wireOp",EDGE,"E448"),sQuery(id+"F12.wireOp",EDGE,"E449"),sQuery(id+"F12.wireOp",EDGE,"E450"),sQuery(id+"F12.wireOp",EDGE,"E451"),sQuery(id+"F12.wireOp",EDGE,"E452"),sQuery(id+"F12.wireOp",EDGE,"E453"),sQuery(id+"F12.wireOp",EDGE,"E454"),sQuery(id+"F12.wireOp",EDGE,"E455"),sQuery(id+"F12.wireOp",EDGE,"E456"),sQuery(id+"F12.wireOp",EDGE,"E457"),sQuery(id+"F12.wireOp",EDGE,"E458"),sQuery(id+"F12.wireOp",EDGE,"E459")])]});
            var Q1;
            Q1=makeQuery(id+"F13.opExtrude","CAP_EDGE",EDGE,{"disambiguationData":[OSD([sQuery(id+"F12.wireOp",EDGE,"E403")])],"isStart":true});
            transform(context, id + "F14", {"entities" : qUnion([Q0]), "transformType" : TransformType.ROTATION, "transformAxis" : qUnion([Q1]), "angle" : 0.26 * radian, "makeCopy" : false});
        }
        {
            var Q0;
            Q0=makeQuery(id+"F13.opExtrude","SWEPT_BODY",BODY,{"disambiguationData":[OSD([sQuery(id+"F12.wireOp",EDGE,"E259"),sQuery(id+"F12.wireOp",EDGE,"E260"),sQuery(id+"F12.wireOp",EDGE,"E261"),sQuery(id+"F12.wireOp",EDGE,"E262"),sQuery(id+"F12.wireOp",EDGE,"E263"),sQuery(id+"F12.wireOp",EDGE,"E264"),sQuery(id+"F12.wireOp",EDGE,"E265"),sQuery(id+"F12.wireOp",EDGE,"E266"),sQuery(id+"F12.wireOp",EDGE,"E267"),sQuery(id+"F12.wireOp",EDGE,"E268"),sQuery(id+"F12.wireOp",EDGE,"E269"),sQuery(id+"F12.wireOp",EDGE,"E270"),sQuery(id+"F12.wireOp",EDGE,"E271"),sQuery(id+"F12.wireOp",EDGE,"E272"),sQuery(id+"F12.wireOp",EDGE,"E273"),sQuery(id+"F12.wireOp",EDGE,"E274"),sQuery(id+"F12.wireOp",EDGE,"E275"),sQuery(id+"F12.wireOp",EDGE,"E276"),sQuery(id+"F12.wireOp",EDGE,"E277"),sQuery(id+"F12.wireOp",EDGE,"E278"),sQuery(id+"F12.wireOp",EDGE,"E279"),sQuery(id+"F12.wireOp",EDGE,"E280"),sQuery(id+"F12.wireOp",EDGE,"E281"),sQuery(id+"F12.wireOp",EDGE,"E282"),sQuery(id+"F12.wireOp",EDGE,"E283"),sQuery(id+"F12.wireOp",EDGE,"E284"),sQuery(id+"F12.wireOp",EDGE,"E285"),sQuery(id+"F12.wireOp",EDGE,"E286"),sQuery(id+"F12.wireOp",EDGE,"E287"),sQuery(id+"F12.wireOp",EDGE,"E288"),sQuery(id+"F12.wireOp",EDGE,"E289"),sQuery(id+"F12.wireOp",EDGE,"E290"),sQuery(id+"F12.wireOp",EDGE,"E291"),sQuery(id+"F12.wireOp",EDGE,"E292"),sQuery(id+"F12.wireOp",EDGE,"E293"),sQuery(id+"F12.wireOp",EDGE,"E294"),sQuery(id+"F12.wireOp",EDGE,"E295"),sQuery(id+"F12.wireOp",EDGE,"E296"),sQuery(id+"F12.wireOp",EDGE,"E297"),sQuery(id+"F12.wireOp",EDGE,"E298"),sQuery(id+"F12.wireOp",EDGE,"E299"),sQuery(id+"F12.wireOp",EDGE,"E300"),sQuery(id+"F12.wireOp",EDGE,"E301"),sQuery(id+"F12.wireOp",EDGE,"E302"),sQuery(id+"F12.wireOp",EDGE,"E303"),sQuery(id+"F12.wireOp",EDGE,"E304"),sQuery(id+"F12.wireOp",EDGE,"E305"),sQuery(id+"F12.wireOp",EDGE,"E306"),sQuery(id+"F12.wireOp",EDGE,"E307"),sQuery(id+"F12.wireOp",EDGE,"E308"),sQuery(id+"F12.wireOp",EDGE,"E309"),sQuery(id+"F12.wireOp",EDGE,"E310"),sQuery(id+"F12.wireOp",EDGE,"E311"),sQuery(id+"F12.wireOp",EDGE,"E312"),sQuery(id+"F12.wireOp",EDGE,"E313"),sQuery(id+"F12.wireOp",EDGE,"E314"),sQuery(id+"F12.wireOp",EDGE,"E315"),sQuery(id+"F12.wireOp",EDGE,"E316"),sQuery(id+"F12.wireOp",EDGE,"E317"),sQuery(id+"F12.wireOp",EDGE,"E318"),sQuery(id+"F12.wireOp",EDGE,"E319"),sQuery(id+"F12.wireOp",EDGE,"E320"),sQuery(id+"F12.wireOp",EDGE,"E321"),sQuery(id+"F12.wireOp",EDGE,"E322"),sQuery(id+"F12.wireOp",EDGE,"E323"),sQuery(id+"F12.wireOp",EDGE,"E324"),sQuery(id+"F12.wireOp",EDGE,"E325"),sQuery(id+"F12.wireOp",EDGE,"E326"),sQuery(id+"F12.wireOp",EDGE,"E327"),sQuery(id+"F12.wireOp",EDGE,"E328"),sQuery(id+"F12.wireOp",EDGE,"E329"),sQuery(id+"F12.wireOp",EDGE,"E330"),sQuery(id+"F12.wireOp",EDGE,"E331"),sQuery(id+"F12.wireOp",EDGE,"E332"),sQuery(id+"F12.wireOp",EDGE,"E333"),sQuery(id+"F12.wireOp",EDGE,"E334"),sQuery(id+"F12.wireOp",EDGE,"E335"),sQuery(id+"F12.wireOp",EDGE,"E336"),sQuery(id+"F12.wireOp",EDGE,"E337"),sQuery(id+"F12.wireOp",EDGE,"E338"),sQuery(id+"F12.wireOp",EDGE,"E339"),sQuery(id+"F12.wireOp",EDGE,"E340"),sQuery(id+"F12.wireOp",EDGE,"E341"),sQuery(id+"F12.wireOp",EDGE,"E342"),sQuery(id+"F12.wireOp",EDGE,"E343"),sQuery(id+"F12.wireOp",EDGE,"E344"),sQuery(id+"F12.wireOp",EDGE,"E345"),sQuery(id+"F12.wireOp",EDGE,"E346"),sQuery(id+"F12.wireOp",EDGE,"E347"),sQuery(id+"F12.wireOp",EDGE,"E348"),sQuery(id+"F12.wireOp",EDGE,"E349"),sQuery(id+"F12.wireOp",EDGE,"E350"),sQuery(id+"F12.wireOp",EDGE,"E351"),sQuery(id+"F12.wireOp",EDGE,"E352"),sQuery(id+"F12.wireOp",EDGE,"E353"),sQuery(id+"F12.wireOp",EDGE,"E354"),sQuery(id+"F12.wireOp",EDGE,"E355"),sQuery(id+"F12.wireOp",EDGE,"E356"),sQuery(id+"F12.wireOp",EDGE,"E357"),sQuery(id+"F12.wireOp",EDGE,"E358"),sQuery(id+"F12.wireOp",EDGE,"E359"),sQuery(id+"F12.wireOp",EDGE,"E360"),sQuery(id+"F12.wireOp",EDGE,"E361"),sQuery(id+"F12.wireOp",EDGE,"E362"),sQuery(id+"F12.wireOp",EDGE,"E363"),sQuery(id+"F12.wireOp",EDGE,"E364"),sQuery(id+"F12.wireOp",EDGE,"E365"),sQuery(id+"F12.wireOp",EDGE,"E366"),sQuery(id+"F12.wireOp",EDGE,"E367"),sQuery(id+"F12.wireOp",EDGE,"E368"),sQuery(id+"F12.wireOp",EDGE,"E369"),sQuery(id+"F12.wireOp",EDGE,"E370"),sQuery(id+"F12.wireOp",EDGE,"E371"),sQuery(id+"F12.wireOp",EDGE,"E372"),sQuery(id+"F12.wireOp",EDGE,"E373"),sQuery(id+"F12.wireOp",EDGE,"E374"),sQuery(id+"F12.wireOp",EDGE,"E375"),sQuery(id+"F12.wireOp",EDGE,"E376"),sQuery(id+"F12.wireOp",EDGE,"E377"),sQuery(id+"F12.wireOp",EDGE,"E378"),sQuery(id+"F12.wireOp",EDGE,"E379"),sQuery(id+"F12.wireOp",EDGE,"E380"),sQuery(id+"F12.wireOp",EDGE,"E381"),sQuery(id+"F12.wireOp",EDGE,"E382"),sQuery(id+"F12.wireOp",EDGE,"E383"),sQuery(id+"F12.wireOp",EDGE,"E384"),sQuery(id+"F12.wireOp",EDGE,"E385"),sQuery(id+"F12.wireOp",EDGE,"E386"),sQuery(id+"F12.wireOp",EDGE,"E387"),sQuery(id+"F12.wireOp",EDGE,"E388"),sQuery(id+"F12.wireOp",EDGE,"E389"),sQuery(id+"F12.wireOp",EDGE,"E390"),sQuery(id+"F12.wireOp",EDGE,"E391"),sQuery(id+"F12.wireOp",EDGE,"E392"),sQuery(id+"F12.wireOp",EDGE,"E393"),sQuery(id+"F12.wireOp",EDGE,"E394"),sQuery(id+"F12.wireOp",EDGE,"E395"),sQuery(id+"F12.wireOp",EDGE,"E396"),sQuery(id+"F12.wireOp",EDGE,"E397"),sQuery(id+"F12.wireOp",EDGE,"E398"),sQuery(id+"F12.wireOp",EDGE,"E399"),sQuery(id+"F12.wireOp",EDGE,"E400"),sQuery(id+"F12.wireOp",EDGE,"E401"),sQuery(id+"F12.wireOp",EDGE,"E402"),sQuery(id+"F12.wireOp",EDGE,"E403"),sQuery(id+"F12.wireOp",EDGE,"E404"),sQuery(id+"F12.wireOp",EDGE,"E405"),sQuery(id+"F12.wireOp",EDGE,"E406"),sQuery(id+"F12.wireOp",EDGE,"E407"),sQuery(id+"F12.wireOp",EDGE,"E408"),sQuery(id+"F12.wireOp",EDGE,"E409"),sQuery(id+"F12.wireOp",EDGE,"E410"),sQuery(id+"F12.wireOp",EDGE,"E411"),sQuery(id+"F12.wireOp",EDGE,"E412"),sQuery(id+"F12.wireOp",EDGE,"E413"),sQuery(id+"F12.wireOp",EDGE,"E414"),sQuery(id+"F12.wireOp",EDGE,"E415"),sQuery(id+"F12.wireOp",EDGE,"E416"),sQuery(id+"F12.wireOp",EDGE,"E417"),sQuery(id+"F12.wireOp",EDGE,"E418"),sQuery(id+"F12.wireOp",EDGE,"E419"),sQuery(id+"F12.wireOp",EDGE,"E420"),sQuery(id+"F12.wireOp",EDGE,"E421"),sQuery(id+"F12.wireOp",EDGE,"E422"),sQuery(id+"F12.wireOp",EDGE,"E423"),sQuery(id+"F12.wireOp",EDGE,"E424"),sQuery(id+"F12.wireOp",EDGE,"E425"),sQuery(id+"F12.wireOp",EDGE,"E426"),sQuery(id+"F12.wireOp",EDGE,"E427"),sQuery(id+"F12.wireOp",EDGE,"E428"),sQuery(id+"F12.wireOp",EDGE,"E429"),sQuery(id+"F12.wireOp",EDGE,"E430"),sQuery(id+"F12.wireOp",EDGE,"E431"),sQuery(id+"F12.wireOp",EDGE,"E432"),sQuery(id+"F12.wireOp",EDGE,"E433"),sQuery(id+"F12.wireOp",EDGE,"E434"),sQuery(id+"F12.wireOp",EDGE,"E435"),sQuery(id+"F12.wireOp",EDGE,"E436"),sQuery(id+"F12.wireOp",EDGE,"E437"),sQuery(id+"F12.wireOp",EDGE,"E438"),sQuery(id+"F12.wireOp",EDGE,"E439"),sQuery(id+"F12.wireOp",EDGE,"E440"),sQuery(id+"F12.wireOp",EDGE,"E441"),sQuery(id+"F12.wireOp",EDGE,"E442"),sQuery(id+"F12.wireOp",EDGE,"E443"),sQuery(id+"F12.wireOp",EDGE,"E444"),sQuery(id+"F12.wireOp",EDGE,"E445"),sQuery(id+"F12.wireOp",EDGE,"E446"),sQuery(id+"F12.wireOp",EDGE,"E447"),sQuery(id+"F12.wireOp",EDGE,"E448"),sQuery(id+"F12.wireOp",EDGE,"E449"),sQuery(id+"F12.wireOp",EDGE,"E450"),sQuery(id+"F12.wireOp",EDGE,"E451"),sQuery(id+"F12.wireOp",EDGE,"E452"),sQuery(id+"F12.wireOp",EDGE,"E453"),sQuery(id+"F12.wireOp",EDGE,"E454"),sQuery(id+"F12.wireOp",EDGE,"E455"),sQuery(id+"F12.wireOp",EDGE,"E456"),sQuery(id+"F12.wireOp",EDGE,"E457"),sQuery(id+"F12.wireOp",EDGE,"E458"),sQuery(id+"F12.wireOp",EDGE,"E459")])]});
            transform(context, id + "F15", {"entities" : qUnion([Q0]), "transformType" : TransformType.TRANSLATION_3D, "dx" : 271 * mm, "dy" : 152 * mm, "dz" : -39 * mm, "makeCopy" : false});
        }
        {
            var Q0;
            Q0=makeQuery(id+"F6.opExtrude","SWEPT_FACE",FACE,{"disambiguationData":[OSD([sQuery(id+"F5.wireOp",EDGE,"E75.left")])]});
            extrude(context, id + "F16", {"entities" : qUnion([Q0]), "operationType" : NewBodyOperationType.ADD, "depth" : 161 * mm, "offsetDistance" : 25 * mm});
        }
    });
